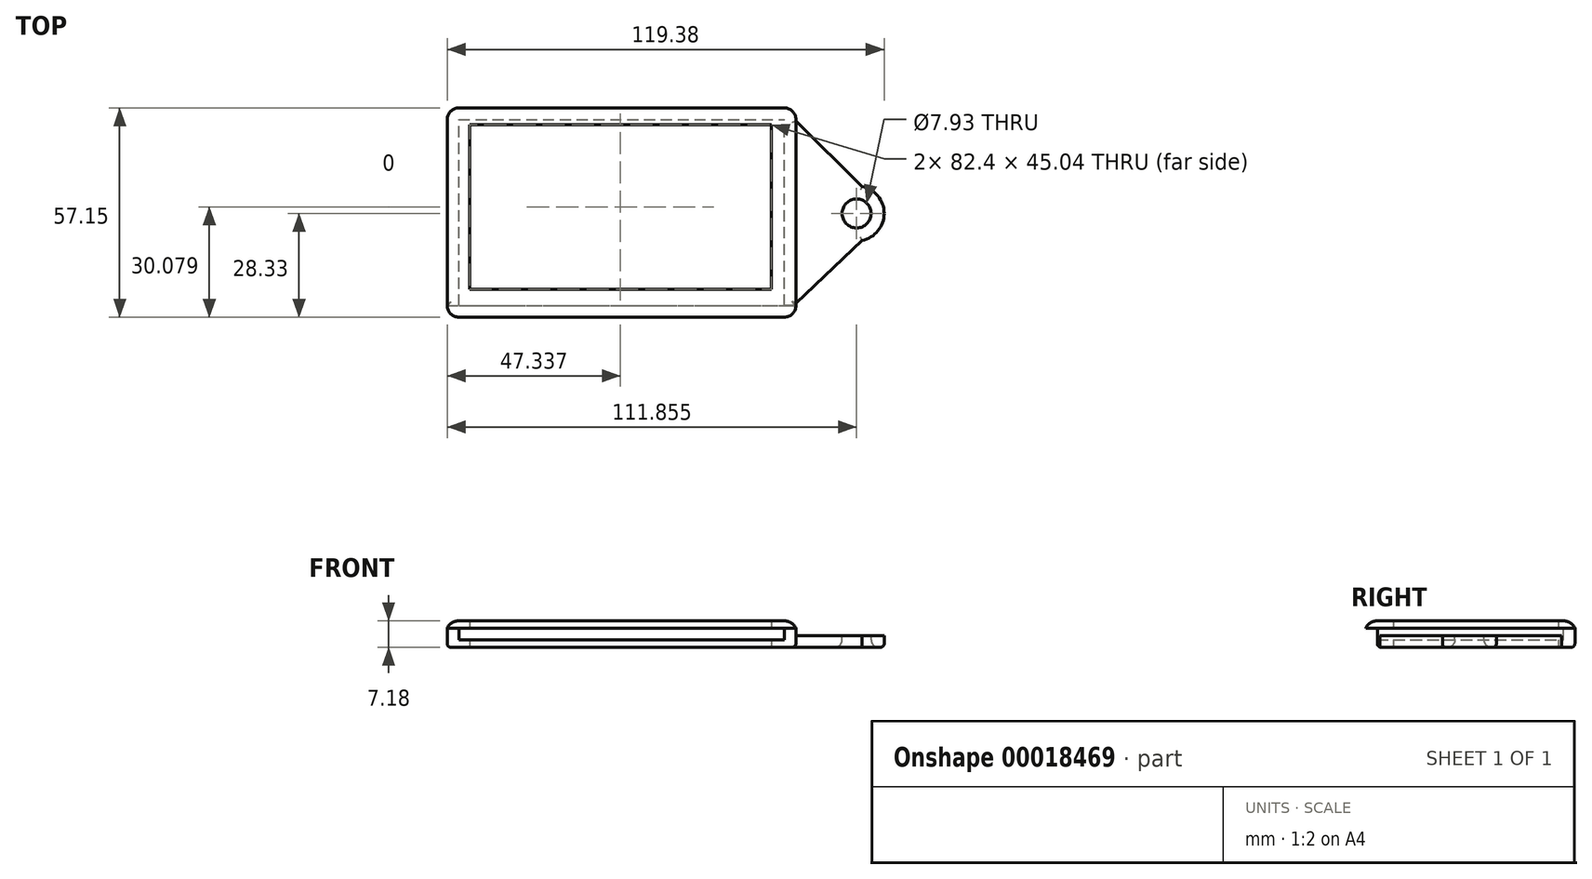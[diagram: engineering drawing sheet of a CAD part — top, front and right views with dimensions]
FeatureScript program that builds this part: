
annotation { "Feature Type Name" : "Feature", "Feature Type Description" : "" }
export const myFeature = defineFeature(function(context is Context, id is Id, definition is map)
    precondition{}
    {
        {
            var Q0;
            Q0=qCreatedBy(makeId("Top.planeOp"),FACE);
            var sketch = newSketch(context, id + "F0", { "sketchPlane" : qUnion([Q0])});
            skLineSegment(sketch, "E0.bottom", {"start": v(60.29, -16.12) * mm, "end": v(-28.61, -16.12) * mm});
            skLineSegment(sketch, "E0.top", {"start": v(60.29, 41.03) * mm, "end": v(-28.61, 41.03) * mm});
            skLineSegment(sketch, "E0.left", {"start": v(63.46, -12.94) * mm, "end": v(63.46, 37.86) * mm});
            skLineSegment(sketch, "E0.right", {"start": v(-31.79, -12.94) * mm, "end": v(-31.79, 37.86) * mm});
            skPoint(sketch, "E1.visualSharp", {"position": v(63.46, -16.12) * mm});
            skArc(sketch, "E1.filletArc", {"start": v(60.29, -16.12) * mm, "mid": v(62.53, -15.19) * mm, "end": v(63.46, -12.94) * mm});
            skPoint(sketch, "E2.visualSharp", {"position": v(-31.79, -16.12) * mm});
            skArc(sketch, "E2.filletArc", {"start": v(-31.79, -12.94) * mm, "mid": v(-30.86, -15.19) * mm, "end": v(-28.61, -16.12) * mm});
            skPoint(sketch, "E3.visualSharp", {"position": v(-31.79, 41.03) * mm});
            skArc(sketch, "E3.filletArc", {"start": v(-28.61, 41.03) * mm, "mid": v(-30.86, 40.1) * mm, "end": v(-31.79, 37.86) * mm});
            skPoint(sketch, "E4.visualSharp", {"position": v(63.46, 41.03) * mm});
            skArc(sketch, "E4.filletArc", {"start": v(63.46, 37.86) * mm, "mid": v(62.53, 40.1) * mm, "end": v(60.29, 41.03) * mm});
            skSolve(sketch);
        }
        {
            var Q0;
            Q0=makeQuery(id+"F0.imprint","IMPRINT",FACE,{"disambiguationData":[TD([[makeQuery(id+"F0.imprint","IMPRINT",EDGE,{"derivedFrom":sQuery(id+"F0.wireOp",EDGE,"E0.bottom")}),-1.0]])]});
            var Q1;
            Q1=makeQuery(id+"F0.imprint","IMPRINT",FACE,{"disambiguationData":[TD([[makeQuery(id+"F0.imprint","IMPRINT",EDGE,{"derivedFrom":sQuery(id+"F0.wireOp",EDGE,"E1.filletArc")}),1.0]])]});
            extrude(context, id + "F1", {"entities" : qUnion([Q0, Q1]), "depth" : 2 * mm});
        }
        {
            var Q0;
            Q0=makeQuery(id+"F1.opExtrude","CAP_FACE",FACE,{"disambiguationData":[OSD([sQuery(id+"F0.wireOp",EDGE,"E1.filletArc"),sQuery(id+"F0.wireOp",EDGE,"E2.filletArc"),sQuery(id+"F0.wireOp",EDGE,"E3.filletArc"),sQuery(id+"F0.wireOp",EDGE,"E4.filletArc"),sQuery(id+"F0.wireOp",EDGE,"E0.bottom"),sQuery(id+"F0.wireOp",EDGE,"E0.top"),sQuery(id+"F0.wireOp",EDGE,"E0.left"),sQuery(id+"F0.wireOp",EDGE,"E0.right")])],"isStart":false});
            fillet(context, id + "F2", {"entities" : qUnion([Q0]), "radius" : 3.17 * mm, "tangentPropagation" : true, "allowEdgeOverflow" : false});
        }
        {
            var Q0;
            Q0=makeQuery(id+"F1.opExtrude","SWEPT_BODY",BODY,{"disambiguationData":[OSD([sQuery(id+"F0.wireOp",EDGE,"E1.filletArc"),sQuery(id+"F0.wireOp",EDGE,"E2.filletArc"),sQuery(id+"F0.wireOp",EDGE,"E3.filletArc"),sQuery(id+"F0.wireOp",EDGE,"E4.filletArc"),sQuery(id+"F0.wireOp",EDGE,"E0.bottom"),sQuery(id+"F0.wireOp",EDGE,"E0.top"),sQuery(id+"F0.wireOp",EDGE,"E0.left"),sQuery(id+"F0.wireOp",EDGE,"E0.right")])]});
            transform(context, id + "F3", {"entities" : qUnion([Q0]), "transformType" : TransformType.TRANSLATION_3D, "dx" : -16.48 * mm, "dy" : -12.22 * mm, "dz" : 0 * mm, "makeCopy" : false});
        }
        {
            var Q0;
            Q0=makeQuery(id+"F1.opExtrude","CAP_FACE",FACE,{"disambiguationData":[OSD([sQuery(id+"F0.wireOp",EDGE,"E1.filletArc"),sQuery(id+"F0.wireOp",EDGE,"E2.filletArc"),sQuery(id+"F0.wireOp",EDGE,"E3.filletArc"),sQuery(id+"F0.wireOp",EDGE,"E4.filletArc"),sQuery(id+"F0.wireOp",EDGE,"E0.bottom"),sQuery(id+"F0.wireOp",EDGE,"E0.top"),sQuery(id+"F0.wireOp",EDGE,"E0.left"),sQuery(id+"F0.wireOp",EDGE,"E0.right")])],"isStart":false});
            var sketch = newSketch(context, id + "F4", { "sketchPlane" : qUnion([Q0])});
            skLineSegment(sketch, "E5", {"start": v(-19.47, 0.13) * mm, "end": v(-18.94, 8.61) * mm});
            skLineSegment(sketch, "E6", {"start": v(-18.94, 8.61) * mm, "end": v(-18.87, 8.63) * mm});
            skLineSegment(sketch, "E7", {"start": v(-18.87, 8.63) * mm, "end": v(-14.96, 8.63) * mm});
            skLineSegment(sketch, "E8", {"start": v(-14.96, 8.63) * mm, "end": v(-14.96, 8.48) * mm});
            skLineSegment(sketch, "E9", {"start": v(-14.96, 8.48) * mm, "end": v(-15.8, 0.4) * mm});
            skLineSegment(sketch, "E10", {"start": v(-15.8, 0.4) * mm, "end": v(-15.77, 0.38) * mm});
            skLineSegment(sketch, "E11", {"start": v(-15.77, 0.38) * mm, "end": v(-13.92, 0.52) * mm});
            skLineSegment(sketch, "E12", {"start": v(-13.92, 0.52) * mm, "end": v(-13.91, 0.56) * mm});
            skLineSegment(sketch, "E13", {"start": v(-13.91, 0.56) * mm, "end": v(-13.91, 3.27) * mm});
            skLineSegment(sketch, "E14", {"start": v(-13.91, 3.27) * mm, "end": v(-13.9, 3.67) * mm});
            skLineSegment(sketch, "E15", {"start": v(-13.9, 3.67) * mm, "end": v(-13.87, 4.23) * mm});
            skLineSegment(sketch, "E16", {"start": v(-13.87, 4.23) * mm, "end": v(-13.82, 4.74) * mm});
            skLineSegment(sketch, "E17", {"start": v(-13.82, 4.74) * mm, "end": v(-13.73, 5.21) * mm});
            skLineSegment(sketch, "E18", {"start": v(-13.73, 5.21) * mm, "end": v(-13.63, 5.65) * mm});
            skLineSegment(sketch, "E19", {"start": v(-13.63, 5.65) * mm, "end": v(-13.5, 6.04) * mm});
            skLineSegment(sketch, "E20", {"start": v(-13.5, 6.04) * mm, "end": v(-13.36, 6.4) * mm});
            skLineSegment(sketch, "E21", {"start": v(-13.36, 6.4) * mm, "end": v(-13.2, 6.73) * mm});
            skLineSegment(sketch, "E22", {"start": v(-13.2, 6.73) * mm, "end": v(-13.03, 7.02) * mm});
            skLineSegment(sketch, "E23", {"start": v(-13.03, 7.02) * mm, "end": v(-12.85, 7.28) * mm});
            skLineSegment(sketch, "E24", {"start": v(-12.85, 7.28) * mm, "end": v(-12.65, 7.5) * mm});
            skLineSegment(sketch, "E25", {"start": v(-12.65, 7.5) * mm, "end": v(-12.45, 7.71) * mm});
            skLineSegment(sketch, "E26", {"start": v(-12.45, 7.71) * mm, "end": v(-12.24, 7.9) * mm});
            skLineSegment(sketch, "E27", {"start": v(-12.24, 7.9) * mm, "end": v(-12.03, 8.05) * mm});
            skLineSegment(sketch, "E28", {"start": v(-12.03, 8.05) * mm, "end": v(-11.81, 8.18) * mm});
            skLineSegment(sketch, "E29", {"start": v(-11.81, 8.18) * mm, "end": v(-11.6, 8.29) * mm});
            skLineSegment(sketch, "E30", {"start": v(-11.6, 8.29) * mm, "end": v(-11.39, 8.38) * mm});
            skLineSegment(sketch, "E31", {"start": v(-11.39, 8.38) * mm, "end": v(-11.18, 8.45) * mm});
            skLineSegment(sketch, "E32", {"start": v(-11.18, 8.45) * mm, "end": v(-10.98, 8.51) * mm});
            skLineSegment(sketch, "E33", {"start": v(-10.98, 8.51) * mm, "end": v(-10.78, 8.56) * mm});
            skLineSegment(sketch, "E34", {"start": v(-10.78, 8.56) * mm, "end": v(-10.6, 8.59) * mm});
            skLineSegment(sketch, "E35", {"start": v(-10.6, 8.59) * mm, "end": v(-10.43, 8.61) * mm});
            skLineSegment(sketch, "E36", {"start": v(-10.43, 8.61) * mm, "end": v(-10.27, 8.63) * mm});
            skLineSegment(sketch, "E37", {"start": v(-10.27, 8.63) * mm, "end": v(-9.72, 8.63) * mm});
            skLineSegment(sketch, "E38", {"start": v(-9.72, 8.63) * mm, "end": v(-2.96, 8.63) * mm});
            skLineSegment(sketch, "E39", {"start": v(-2.96, 8.63) * mm, "end": v(-2.92, 8.55) * mm});
            skLineSegment(sketch, "E40", {"start": v(-2.92, 8.55) * mm, "end": v(-2.92, 1.78) * mm});
            skLineSegment(sketch, "E41", {"start": v(-2.92, 1.78) * mm, "end": v(-2.73, 1.8) * mm});
            skLineSegment(sketch, "E42", {"start": v(-2.73, 1.8) * mm, "end": v(-1.76, 1.95) * mm});
            skLineSegment(sketch, "E43", {"start": v(-1.76, 1.95) * mm, "end": v(-1.69, 2.11) * mm});
            skLineSegment(sketch, "E44", {"start": v(-1.69, 2.11) * mm, "end": v(-1.7, 2.42) * mm});
            skLineSegment(sketch, "E45", {"start": v(-1.7, 2.42) * mm, "end": v(-1.7, 2.74) * mm});
            skLineSegment(sketch, "E46", {"start": v(-1.7, 2.74) * mm, "end": v(-1.7, 3.08) * mm});
            skLineSegment(sketch, "E47", {"start": v(-1.7, 3.08) * mm, "end": v(-1.68, 3.43) * mm});
            skLineSegment(sketch, "E48", {"start": v(-1.68, 3.43) * mm, "end": v(-1.66, 3.78) * mm});
            skLineSegment(sketch, "E49", {"start": v(-1.66, 3.78) * mm, "end": v(-1.62, 4.15) * mm});
            skLineSegment(sketch, "E50", {"start": v(-1.62, 4.15) * mm, "end": v(-1.57, 4.51) * mm});
            skLineSegment(sketch, "E51", {"start": v(-1.57, 4.51) * mm, "end": v(-1.5, 4.88) * mm});
            skLineSegment(sketch, "E52", {"start": v(-1.5, 4.88) * mm, "end": v(-1.42, 5.25) * mm});
            skLineSegment(sketch, "E53", {"start": v(-1.42, 5.25) * mm, "end": v(-1.3, 5.6) * mm});
            skLineSegment(sketch, "E54", {"start": v(-1.3, 5.6) * mm, "end": v(-1.18, 5.96) * mm});
            skLineSegment(sketch, "E55", {"start": v(-1.18, 5.96) * mm, "end": v(-1.02, 6.3) * mm});
            skLineSegment(sketch, "E56", {"start": v(-1.02, 6.3) * mm, "end": v(-0.84, 6.63) * mm});
            skLineSegment(sketch, "E57", {"start": v(-0.84, 6.63) * mm, "end": v(-0.63, 6.94) * mm});
            skLineSegment(sketch, "E58", {"start": v(-0.63, 6.94) * mm, "end": v(-0.4, 7.24) * mm});
            skLineSegment(sketch, "E59", {"start": v(-0.4, 7.24) * mm, "end": v(-0.12, 7.5) * mm});
            skLineSegment(sketch, "E60", {"start": v(-0.12, 7.5) * mm, "end": v(0.19, 7.76) * mm});
            skLineSegment(sketch, "E61", {"start": v(0.19, 7.76) * mm, "end": v(0.53, 7.98) * mm});
            skLineSegment(sketch, "E62", {"start": v(0.53, 7.98) * mm, "end": v(0.91, 8.17) * mm});
            skLineSegment(sketch, "E63", {"start": v(0.91, 8.17) * mm, "end": v(1.33, 8.33) * mm});
            skLineSegment(sketch, "E64", {"start": v(1.33, 8.33) * mm, "end": v(1.8, 8.45) * mm});
            skLineSegment(sketch, "E65", {"start": v(1.8, 8.45) * mm, "end": v(2.3, 8.54) * mm});
            skLineSegment(sketch, "E66", {"start": v(2.3, 8.54) * mm, "end": v(2.86, 8.58) * mm});
            skLineSegment(sketch, "E67", {"start": v(2.86, 8.58) * mm, "end": v(3.44, 8.58) * mm});
            skLineSegment(sketch, "E68", {"start": v(3.44, 8.58) * mm, "end": v(3.97, 8.53) * mm});
            skLineSegment(sketch, "E69", {"start": v(3.97, 8.53) * mm, "end": v(4.45, 8.43) * mm});
            skLineSegment(sketch, "E70", {"start": v(4.45, 8.43) * mm, "end": v(4.9, 8.29) * mm});
            skLineSegment(sketch, "E71", {"start": v(4.9, 8.29) * mm, "end": v(5.28, 8.1) * mm});
            skLineSegment(sketch, "E72", {"start": v(5.28, 8.1) * mm, "end": v(5.64, 7.89) * mm});
            skLineSegment(sketch, "E73", {"start": v(5.64, 7.89) * mm, "end": v(5.95, 7.64) * mm});
            skLineSegment(sketch, "E74", {"start": v(5.95, 7.64) * mm, "end": v(6.22, 7.37) * mm});
            skLineSegment(sketch, "E75", {"start": v(6.22, 7.37) * mm, "end": v(6.47, 7.08) * mm});
            skLineSegment(sketch, "E76", {"start": v(6.47, 7.08) * mm, "end": v(6.67, 6.78) * mm});
            skLineSegment(sketch, "E77", {"start": v(6.67, 6.78) * mm, "end": v(6.85, 6.46) * mm});
            skLineSegment(sketch, "E78", {"start": v(6.85, 6.46) * mm, "end": v(7, 6.13) * mm});
            skLineSegment(sketch, "E79", {"start": v(7, 6.13) * mm, "end": v(7.13, 5.8) * mm});
            skLineSegment(sketch, "E80", {"start": v(7.13, 5.8) * mm, "end": v(7.23, 5.48) * mm});
            skLineSegment(sketch, "E81", {"start": v(7.23, 5.48) * mm, "end": v(7.31, 5.16) * mm});
            skLineSegment(sketch, "E82", {"start": v(7.31, 5.16) * mm, "end": v(7.37, 4.85) * mm});
            skLineSegment(sketch, "E83", {"start": v(7.37, 4.85) * mm, "end": v(7.42, 4.56) * mm});
            skLineSegment(sketch, "E84", {"start": v(7.42, 4.56) * mm, "end": v(7.45, 4.29) * mm});
            skLineSegment(sketch, "E85", {"start": v(7.45, 4.29) * mm, "end": v(7.47, 4.04) * mm});
            skLineSegment(sketch, "E86", {"start": v(7.47, 4.04) * mm, "end": v(7.48, 3.82) * mm});
            skLineSegment(sketch, "E87", {"start": v(7.48, 3.82) * mm, "end": v(7.49, 3.64) * mm});
            skLineSegment(sketch, "E88", {"start": v(7.49, 3.64) * mm, "end": v(7.48, 3.34) * mm});
            skLineSegment(sketch, "E89", {"start": v(7.48, 3.34) * mm, "end": v(7.5, 3.34) * mm});
            skLineSegment(sketch, "E90", {"start": v(7.5, 3.34) * mm, "end": v(9.28, 3.68) * mm});
            skLineSegment(sketch, "E91", {"start": v(9.28, 3.68) * mm, "end": v(9.3, 3.72) * mm});
            skLineSegment(sketch, "E92", {"start": v(9.3, 3.72) * mm, "end": v(8.78, 8.57) * mm});
            skLineSegment(sketch, "E93", {"start": v(8.78, 8.57) * mm, "end": v(8.8, 8.63) * mm});
            skLineSegment(sketch, "E94", {"start": v(8.8, 8.63) * mm, "end": v(12.67, 8.63) * mm});
            skLineSegment(sketch, "E95", {"start": v(12.67, 8.63) * mm, "end": v(12.73, 8.6) * mm});
            skLineSegment(sketch, "E96", {"start": v(12.73, 8.6) * mm, "end": v(13, 4.29) * mm});
            skLineSegment(sketch, "E97", {"start": v(13, 4.29) * mm, "end": v(13, 4.22) * mm});
            skLineSegment(sketch, "E98", {"start": v(13, 4.22) * mm, "end": v(14.22, 4.4) * mm});
            skLineSegment(sketch, "E99", {"start": v(14.22, 4.4) * mm, "end": v(14.24, 4.41) * mm});
            skLineSegment(sketch, "E100", {"start": v(14.24, 4.41) * mm, "end": v(14.43, 8.56) * mm});
            skLineSegment(sketch, "E101", {"start": v(14.43, 8.56) * mm, "end": v(14.45, 8.63) * mm});
            skLineSegment(sketch, "E102", {"start": v(14.45, 8.63) * mm, "end": v(18.42, 8.63) * mm});
            skLineSegment(sketch, "E103", {"start": v(18.42, 8.63) * mm, "end": v(18.5, 8.62) * mm});
            skLineSegment(sketch, "E104", {"start": v(18.5, 8.62) * mm, "end": v(18.13, 5.15) * mm});
            skLineSegment(sketch, "E105", {"start": v(18.13, 5.15) * mm, "end": v(18.14, 5.08) * mm});
            skLineSegment(sketch, "E106", {"start": v(18.14, 5.08) * mm, "end": v(24.47, 6.16) * mm});
            skLineSegment(sketch, "E107", {"start": v(24.47, 6.16) * mm, "end": v(24.6, 6.19) * mm});
            skLineSegment(sketch, "E108", {"start": v(24.6, 6.19) * mm, "end": v(24.6, 8.58) * mm});
            skLineSegment(sketch, "E109", {"start": v(24.6, 8.58) * mm, "end": v(24.61, 8.63) * mm});
            skLineSegment(sketch, "E110", {"start": v(24.61, 8.63) * mm, "end": v(29.13, 8.63) * mm});
            skLineSegment(sketch, "E111", {"start": v(29.13, 8.63) * mm, "end": v(29.23, 8.63) * mm});
            skLineSegment(sketch, "E112", {"start": v(29.23, 8.63) * mm, "end": v(29.23, 7.04) * mm});
            skLineSegment(sketch, "E113", {"start": v(29.23, 7.04) * mm, "end": v(30.8, 7.38) * mm});
            skLineSegment(sketch, "E114", {"start": v(30.8, 7.38) * mm, "end": v(30.84, 7.39) * mm});
            skLineSegment(sketch, "E115", {"start": v(30.84, 7.39) * mm, "end": v(30.84, 14.86) * mm});
            skLineSegment(sketch, "E116", {"start": v(30.84, 14.86) * mm, "end": v(30.81, 15.07) * mm});
            skLineSegment(sketch, "E117", {"start": v(30.81, 15.07) * mm, "end": v(-32.69, 15.07) * mm});
            skLineSegment(sketch, "E118", {"start": v(-32.69, 15.07) * mm, "end": v(-32.74, 6.1) * mm});
            skLineSegment(sketch, "E119", {"start": v(-32.74, 6.1) * mm, "end": v(-32.73, 5.93) * mm});
            skLineSegment(sketch, "E120", {"start": v(-32.73, 5.93) * mm, "end": v(-32.7, 5.75) * mm});
            skLineSegment(sketch, "E121", {"start": v(-32.7, 5.75) * mm, "end": v(-32.67, 5.57) * mm});
            skLineSegment(sketch, "E122", {"start": v(-32.67, 5.57) * mm, "end": v(-32.62, 5.4) * mm});
            skLineSegment(sketch, "E123", {"start": v(-32.62, 5.4) * mm, "end": v(-32.56, 5.22) * mm});
            skLineSegment(sketch, "E124", {"start": v(-32.56, 5.22) * mm, "end": v(-32.48, 5.04) * mm});
            skLineSegment(sketch, "E125", {"start": v(-32.48, 5.04) * mm, "end": v(-32.4, 4.87) * mm});
            skLineSegment(sketch, "E126", {"start": v(-32.4, 4.87) * mm, "end": v(-32.31, 4.7) * mm});
            skLineSegment(sketch, "E127", {"start": v(-32.31, 4.7) * mm, "end": v(-32.22, 4.53) * mm});
            skLineSegment(sketch, "E128", {"start": v(-32.22, 4.53) * mm, "end": v(-32.12, 4.37) * mm});
            skLineSegment(sketch, "E129", {"start": v(-32.12, 4.37) * mm, "end": v(-32.02, 4.21) * mm});
            skLineSegment(sketch, "E130", {"start": v(-32.02, 4.21) * mm, "end": v(-31.92, 4.06) * mm});
            skLineSegment(sketch, "E131", {"start": v(-31.92, 4.06) * mm, "end": v(-31.82, 3.92) * mm});
            skLineSegment(sketch, "E132", {"start": v(-31.82, 3.92) * mm, "end": v(-31.72, 3.79) * mm});
            skLineSegment(sketch, "E133", {"start": v(-31.72, 3.79) * mm, "end": v(-31.53, 3.55) * mm});
            skLineSegment(sketch, "E134", {"start": v(-31.53, 3.55) * mm, "end": v(-31.36, 3.35) * mm});
            skLineSegment(sketch, "E135", {"start": v(-31.36, 3.35) * mm, "end": v(-31.1, 3.08) * mm});
            skLineSegment(sketch, "E136", {"start": v(-31.1, 3.08) * mm, "end": v(-31, 3.08) * mm});
            skLineSegment(sketch, "E137", {"start": v(-31, 3.08) * mm, "end": v(-30.99, 8.63) * mm});
            skLineSegment(sketch, "E138", {"start": v(-30.99, 8.63) * mm, "end": v(-27.17, 8.63) * mm});
            skLineSegment(sketch, "E139", {"start": v(-27.17, 8.63) * mm, "end": v(-27.17, 1.68) * mm});
            skLineSegment(sketch, "E140", {"start": v(-27.17, 1.68) * mm, "end": v(-26.96, 0.75) * mm});
            skLineSegment(sketch, "E141", {"start": v(-26.96, 0.75) * mm, "end": v(-23.9, 0.36) * mm});
            skLineSegment(sketch, "E142", {"start": v(-23.9, 0.36) * mm, "end": v(-25, 8.63) * mm});
            skLineSegment(sketch, "E143", {"start": v(-25, 8.63) * mm, "end": v(-24.9, 8.63) * mm});
            skLineSegment(sketch, "E144", {"start": v(-24.9, 8.63) * mm, "end": v(-20.71, 8.63) * mm});
            skLineSegment(sketch, "E145", {"start": v(-20.71, 8.63) * mm, "end": v(-20.7, 8.44) * mm});
            skLineSegment(sketch, "E146", {"start": v(-20.7, 8.44) * mm, "end": v(-20.23, 0.14) * mm});
            skLineSegment(sketch, "E147", {"start": v(-20.23, 0.14) * mm, "end": v(-20.22, 0.13) * mm});
            skLineSegment(sketch, "E148", {"start": v(-20.22, 0.13) * mm, "end": v(-19.47, 0.13) * mm});
            skLineSegment(sketch, "E149", {"start": v(-20.02, -2.51) * mm, "end": v(-19.21, -2.5) * mm});
            skLineSegment(sketch, "E150", {"start": v(-19.21, -2.5) * mm, "end": v(-16.96, -2.41) * mm});
            skLineSegment(sketch, "E151", {"start": v(-16.96, -2.41) * mm, "end": v(-16.7, -2.4) * mm});
            skLineSegment(sketch, "E152", {"start": v(-16.7, -2.4) * mm, "end": v(-14.72, -2.33) * mm});
            skLineSegment(sketch, "E153", {"start": v(-14.72, -2.33) * mm, "end": v(-12.56, -2.21) * mm});
            skLineSegment(sketch, "E154", {"start": v(-12.56, -2.21) * mm, "end": v(-10.25, -2.05) * mm});
            skLineSegment(sketch, "E155", {"start": v(-10.25, -2.05) * mm, "end": v(-7.8, -1.84) * mm});
            skLineSegment(sketch, "E156", {"start": v(-7.8, -1.84) * mm, "end": v(-5.23, -1.6) * mm});
            skLineSegment(sketch, "E157", {"start": v(-5.23, -1.6) * mm, "end": v(-2.58, -1.34) * mm});
            skLineSegment(sketch, "E158", {"start": v(-2.58, -1.34) * mm, "end": v(0.14, -1.05) * mm});
            skLineSegment(sketch, "E159", {"start": v(0.14, -1.05) * mm, "end": v(2.9, -0.73) * mm});
            skLineSegment(sketch, "E160", {"start": v(2.9, -0.73) * mm, "end": v(5.67, -0.4) * mm});
            skLineSegment(sketch, "E161", {"start": v(5.67, -0.4) * mm, "end": v(8.44, -0.07) * mm});
            skLineSegment(sketch, "E162", {"start": v(8.44, -0.07) * mm, "end": v(11.18, 0.28) * mm});
            skLineSegment(sketch, "E163", {"start": v(11.18, 0.28) * mm, "end": v(13.86, 0.63) * mm});
            skLineSegment(sketch, "E164", {"start": v(13.86, 0.63) * mm, "end": v(16.47, 0.98) * mm});
            skLineSegment(sketch, "E165", {"start": v(16.47, 0.98) * mm, "end": v(18.97, 1.32) * mm});
            skLineSegment(sketch, "E166", {"start": v(18.97, 1.32) * mm, "end": v(21.35, 1.65) * mm});
            skLineSegment(sketch, "E167", {"start": v(21.35, 1.65) * mm, "end": v(23.58, 1.96) * mm});
            skLineSegment(sketch, "E168", {"start": v(23.58, 1.96) * mm, "end": v(25.63, 2.26) * mm});
            skLineSegment(sketch, "E169", {"start": v(25.63, 2.26) * mm, "end": v(29.13, 2.77) * mm});
            skLineSegment(sketch, "E170", {"start": v(29.13, 2.77) * mm, "end": v(33.18, 3.38) * mm});
            skLineSegment(sketch, "E171", {"start": v(33.18, 3.38) * mm, "end": v(33.32, 3.45) * mm});
            skLineSegment(sketch, "E172", {"start": v(33.32, 3.45) * mm, "end": v(33.44, 3.55) * mm});
            skLineSegment(sketch, "E173", {"start": v(33.44, 3.55) * mm, "end": v(33.54, 3.66) * mm});
            skLineSegment(sketch, "E174", {"start": v(33.54, 3.66) * mm, "end": v(33.64, 3.8) * mm});
            skLineSegment(sketch, "E175", {"start": v(33.64, 3.8) * mm, "end": v(33.71, 3.95) * mm});
            skLineSegment(sketch, "E176", {"start": v(33.71, 3.95) * mm, "end": v(33.78, 4.1) * mm});
            skLineSegment(sketch, "E177", {"start": v(33.78, 4.1) * mm, "end": v(33.83, 4.28) * mm});
            skLineSegment(sketch, "E178", {"start": v(33.83, 4.28) * mm, "end": v(33.86, 4.46) * mm});
            skLineSegment(sketch, "E179", {"start": v(33.86, 4.46) * mm, "end": v(33.89, 4.65) * mm});
            skLineSegment(sketch, "E180", {"start": v(33.89, 4.65) * mm, "end": v(33.9, 4.84) * mm});
            skLineSegment(sketch, "E181", {"start": v(33.9, 4.84) * mm, "end": v(33.9, 5.02) * mm});
            skLineSegment(sketch, "E182", {"start": v(33.9, 5.02) * mm, "end": v(33.89, 5.21) * mm});
            skLineSegment(sketch, "E183", {"start": v(33.89, 5.21) * mm, "end": v(33.87, 5.4) * mm});
            skLineSegment(sketch, "E184", {"start": v(33.87, 5.4) * mm, "end": v(33.83, 5.57) * mm});
            skLineSegment(sketch, "E185", {"start": v(33.83, 5.57) * mm, "end": v(33.8, 5.74) * mm});
            skLineSegment(sketch, "E186", {"start": v(33.8, 5.74) * mm, "end": v(33.74, 5.9) * mm});
            skLineSegment(sketch, "E187", {"start": v(33.74, 5.9) * mm, "end": v(33.68, 6.04) * mm});
            skLineSegment(sketch, "E188", {"start": v(33.68, 6.04) * mm, "end": v(33.61, 6.17) * mm});
            skLineSegment(sketch, "E189", {"start": v(33.61, 6.17) * mm, "end": v(33.54, 6.28) * mm});
            skLineSegment(sketch, "E190", {"start": v(33.54, 6.28) * mm, "end": v(33.45, 6.37) * mm});
            skLineSegment(sketch, "E191", {"start": v(33.45, 6.37) * mm, "end": v(33.36, 6.43) * mm});
            skLineSegment(sketch, "E192", {"start": v(33.36, 6.43) * mm, "end": v(33.27, 6.47) * mm});
            skLineSegment(sketch, "E193", {"start": v(33.27, 6.47) * mm, "end": v(33.17, 6.48) * mm});
            skLineSegment(sketch, "E194", {"start": v(33.17, 6.48) * mm, "end": v(31.1, 6.08) * mm});
            skLineSegment(sketch, "E195", {"start": v(31.1, 6.08) * mm, "end": v(28.94, 5.66) * mm});
            skLineSegment(sketch, "E196", {"start": v(28.94, 5.66) * mm, "end": v(26.84, 5.26) * mm});
            skLineSegment(sketch, "E197", {"start": v(26.84, 5.26) * mm, "end": v(24.8, 4.87) * mm});
            skLineSegment(sketch, "E198", {"start": v(24.8, 4.87) * mm, "end": v(22.84, 4.5) * mm});
            skLineSegment(sketch, "E199", {"start": v(22.84, 4.5) * mm, "end": v(20.93, 4.16) * mm});
            skLineSegment(sketch, "E200", {"start": v(20.93, 4.16) * mm, "end": v(19.08, 3.83) * mm});
            skLineSegment(sketch, "E201", {"start": v(19.08, 3.83) * mm, "end": v(17.29, 3.51) * mm});
            skLineSegment(sketch, "E202", {"start": v(17.29, 3.51) * mm, "end": v(15.56, 3.21) * mm});
            skLineSegment(sketch, "E203", {"start": v(15.56, 3.21) * mm, "end": v(13.88, 2.92) * mm});
            skLineSegment(sketch, "E204", {"start": v(13.88, 2.92) * mm, "end": v(12.26, 2.65) * mm});
            skLineSegment(sketch, "E205", {"start": v(12.26, 2.65) * mm, "end": v(10.7, 2.4) * mm});
            skLineSegment(sketch, "E206", {"start": v(10.7, 2.4) * mm, "end": v(9.19, 2.15) * mm});
            skLineSegment(sketch, "E207", {"start": v(9.19, 2.15) * mm, "end": v(7.73, 1.91) * mm});
            skLineSegment(sketch, "E208", {"start": v(7.73, 1.91) * mm, "end": v(6.32, 1.7) * mm});
            skLineSegment(sketch, "E209", {"start": v(6.32, 1.7) * mm, "end": v(4.96, 1.48) * mm});
            skLineSegment(sketch, "E210", {"start": v(4.96, 1.48) * mm, "end": v(3.66, 1.28) * mm});
            skLineSegment(sketch, "E211", {"start": v(3.66, 1.28) * mm, "end": v(1.19, 0.92) * mm});
            skLineSegment(sketch, "E212", {"start": v(1.19, 0.92) * mm, "end": v(-1.1, 0.59) * mm});
            skLineSegment(sketch, "E213", {"start": v(-1.1, 0.59) * mm, "end": v(-3.22, 0.3) * mm});
            skLineSegment(sketch, "E214", {"start": v(-3.22, 0.3) * mm, "end": v(-4.2, 0.15) * mm});
            skLineSegment(sketch, "E215", {"start": v(-4.2, 0.15) * mm, "end": v(-6.21, -0.14) * mm});
            skLineSegment(sketch, "E216", {"start": v(-6.21, -0.14) * mm, "end": v(-8.47, -0.45) * mm});
            skLineSegment(sketch, "E217", {"start": v(-8.47, -0.45) * mm, "end": v(-10.62, -0.71) * mm});
            skLineSegment(sketch, "E218", {"start": v(-10.62, -0.71) * mm, "end": v(-12.67, -0.93) * mm});
            skLineSegment(sketch, "E219", {"start": v(-12.67, -0.93) * mm, "end": v(-14.6, -1.11) * mm});
            skLineSegment(sketch, "E220", {"start": v(-14.6, -1.11) * mm, "end": v(-16.45, -1.25) * mm});
            skLineSegment(sketch, "E221", {"start": v(-16.45, -1.25) * mm, "end": v(-18.18, -1.34) * mm});
            skLineSegment(sketch, "E222", {"start": v(-18.18, -1.34) * mm, "end": v(-19.82, -1.38) * mm});
            skLineSegment(sketch, "E223", {"start": v(-19.82, -1.38) * mm, "end": v(-21.36, -1.38) * mm});
            skLineSegment(sketch, "E224", {"start": v(-21.36, -1.38) * mm, "end": v(-22.8, -1.33) * mm});
            skLineSegment(sketch, "E225", {"start": v(-22.8, -1.33) * mm, "end": v(-24.15, -1.24) * mm});
            skLineSegment(sketch, "E226", {"start": v(-24.15, -1.24) * mm, "end": v(-25.4, -1.1) * mm});
            skLineSegment(sketch, "E227", {"start": v(-25.4, -1.1) * mm, "end": v(-26.57, -0.92) * mm});
            skLineSegment(sketch, "E228", {"start": v(-26.57, -0.92) * mm, "end": v(-27.64, -0.68) * mm});
            skLineSegment(sketch, "E229", {"start": v(-27.64, -0.68) * mm, "end": v(-28.62, -0.4) * mm});
            skLineSegment(sketch, "E230", {"start": v(-28.62, -0.4) * mm, "end": v(-29.51, -0.07) * mm});
            skLineSegment(sketch, "E231", {"start": v(-29.51, -0.07) * mm, "end": v(-30.32, 0.3) * mm});
            skLineSegment(sketch, "E232", {"start": v(-30.32, 0.3) * mm, "end": v(-31.04, 0.73) * mm});
            skLineSegment(sketch, "E233", {"start": v(-31.04, 0.73) * mm, "end": v(-31.67, 1.2) * mm});
            skLineSegment(sketch, "E234", {"start": v(-31.67, 1.2) * mm, "end": v(-32.22, 1.72) * mm});
            skLineSegment(sketch, "E235", {"start": v(-32.22, 1.72) * mm, "end": v(-32.7, 2.3) * mm});
            skLineSegment(sketch, "E236", {"start": v(-32.7, 2.3) * mm, "end": v(-33.08, 2.92) * mm});
            skLineSegment(sketch, "E237", {"start": v(-33.08, 2.92) * mm, "end": v(-33.4, 3.6) * mm});
            skLineSegment(sketch, "E238", {"start": v(-33.4, 3.6) * mm, "end": v(-33.63, 4.32) * mm});
            skLineSegment(sketch, "E239", {"start": v(-33.63, 4.32) * mm, "end": v(-33.7, 4.4) * mm});
            skLineSegment(sketch, "E240", {"start": v(-33.7, 4.4) * mm, "end": v(-33.68, 4.06) * mm});
            skLineSegment(sketch, "E241", {"start": v(-33.68, 4.06) * mm, "end": v(-33.64, 3.74) * mm});
            skLineSegment(sketch, "E242", {"start": v(-33.64, 3.74) * mm, "end": v(-33.58, 3.43) * mm});
            skLineSegment(sketch, "E243", {"start": v(-33.58, 3.43) * mm, "end": v(-33.5, 3.12) * mm});
            skLineSegment(sketch, "E244", {"start": v(-33.5, 3.12) * mm, "end": v(-33.4, 2.82) * mm});
            skLineSegment(sketch, "E245", {"start": v(-33.4, 2.82) * mm, "end": v(-33.28, 2.53) * mm});
            skLineSegment(sketch, "E246", {"start": v(-33.28, 2.53) * mm, "end": v(-33.14, 2.24) * mm});
            skLineSegment(sketch, "E247", {"start": v(-33.14, 2.24) * mm, "end": v(-32.98, 1.97) * mm});
            skLineSegment(sketch, "E248", {"start": v(-32.98, 1.97) * mm, "end": v(-32.8, 1.7) * mm});
            skLineSegment(sketch, "E249", {"start": v(-32.8, 1.7) * mm, "end": v(-32.62, 1.44) * mm});
            skLineSegment(sketch, "E250", {"start": v(-32.62, 1.44) * mm, "end": v(-32.41, 1.2) * mm});
            skLineSegment(sketch, "E251", {"start": v(-32.41, 1.2) * mm, "end": v(-32.2, 0.95) * mm});
            skLineSegment(sketch, "E252", {"start": v(-32.2, 0.95) * mm, "end": v(-31.97, 0.72) * mm});
            skLineSegment(sketch, "E253", {"start": v(-31.97, 0.72) * mm, "end": v(-31.73, 0.5) * mm});
            skLineSegment(sketch, "E254", {"start": v(-31.73, 0.5) * mm, "end": v(-31.48, 0.3) * mm});
            skLineSegment(sketch, "E255", {"start": v(-31.48, 0.3) * mm, "end": v(-31.22, 0.09) * mm});
            skLineSegment(sketch, "E256", {"start": v(-31.22, 0.09) * mm, "end": v(-30.95, -0.1) * mm});
            skLineSegment(sketch, "E257", {"start": v(-30.95, -0.1) * mm, "end": v(-30.67, -0.28) * mm});
            skLineSegment(sketch, "E258", {"start": v(-30.67, -0.28) * mm, "end": v(-30.4, -0.45) * mm});
            skLineSegment(sketch, "E259", {"start": v(-30.4, -0.45) * mm, "end": v(-30.1, -0.61) * mm});
            skLineSegment(sketch, "E260", {"start": v(-30.1, -0.61) * mm, "end": v(-29.81, -0.76) * mm});
            skLineSegment(sketch, "E261", {"start": v(-29.81, -0.76) * mm, "end": v(-29.52, -0.9) * mm});
            skLineSegment(sketch, "E262", {"start": v(-29.52, -0.9) * mm, "end": v(-29.22, -1.03) * mm});
            skLineSegment(sketch, "E263", {"start": v(-29.22, -1.03) * mm, "end": v(-28.74, -1.22) * mm});
            skLineSegment(sketch, "E264", {"start": v(-28.74, -1.22) * mm, "end": v(-28.52, -1.3) * mm});
            skLineSegment(sketch, "E265", {"start": v(-28.52, -1.3) * mm, "end": v(-28.3, -1.38) * mm});
            skLineSegment(sketch, "E266", {"start": v(-28.3, -1.38) * mm, "end": v(-28.08, -1.45) * mm});
            skLineSegment(sketch, "E267", {"start": v(-28.08, -1.45) * mm, "end": v(-27.85, -1.52) * mm});
            skLineSegment(sketch, "E268", {"start": v(-27.85, -1.52) * mm, "end": v(-27.63, -1.6) * mm});
            skLineSegment(sketch, "E269", {"start": v(-27.63, -1.6) * mm, "end": v(-27.41, -1.66) * mm});
            skLineSegment(sketch, "E270", {"start": v(-27.41, -1.66) * mm, "end": v(-26.97, -1.77) * mm});
            skLineSegment(sketch, "E271", {"start": v(-26.97, -1.77) * mm, "end": v(-26.52, -1.88) * mm});
            skLineSegment(sketch, "E272", {"start": v(-26.52, -1.88) * mm, "end": v(-26.07, -1.98) * mm});
            skLineSegment(sketch, "E273", {"start": v(-26.07, -1.98) * mm, "end": v(-25.61, -2.07) * mm});
            skLineSegment(sketch, "E274", {"start": v(-25.61, -2.07) * mm, "end": v(-25.15, -2.15) * mm});
            skLineSegment(sketch, "E275", {"start": v(-25.15, -2.15) * mm, "end": v(-24.69, -2.22) * mm});
            skLineSegment(sketch, "E276", {"start": v(-24.69, -2.22) * mm, "end": v(-24.22, -2.28) * mm});
            skLineSegment(sketch, "E277", {"start": v(-24.22, -2.28) * mm, "end": v(-23.51, -2.37) * mm});
            skLineSegment(sketch, "E278", {"start": v(-23.51, -2.37) * mm, "end": v(-22.73, -2.42) * mm});
            skLineSegment(sketch, "E279", {"start": v(-22.73, -2.42) * mm, "end": v(-21.7, -2.47) * mm});
            skLineSegment(sketch, "E280", {"start": v(-21.7, -2.47) * mm, "end": v(-20.75, -2.5) * mm});
            skLineSegment(sketch, "E281", {"start": v(-20.75, -2.5) * mm, "end": v(-20.2, -2.51) * mm});
            skLineSegment(sketch, "E282", {"start": v(-20.2, -2.51) * mm, "end": v(-20.02, -2.51) * mm});
            skLineSegment(sketch, "E283", {"start": v(2.46, 2.56) * mm, "end": v(3.5, 2.72) * mm});
            skLineSegment(sketch, "E284", {"start": v(3.5, 2.72) * mm, "end": v(3.5, 3.94) * mm});
            skLineSegment(sketch, "E285", {"start": v(3.5, 3.94) * mm, "end": v(3.5, 4.05) * mm});
            skLineSegment(sketch, "E286", {"start": v(3.5, 4.05) * mm, "end": v(3.48, 4.17) * mm});
            skLineSegment(sketch, "E287", {"start": v(3.48, 4.17) * mm, "end": v(3.46, 4.3) * mm});
            skLineSegment(sketch, "E288", {"start": v(3.46, 4.3) * mm, "end": v(3.43, 4.42) * mm});
            skLineSegment(sketch, "E289", {"start": v(3.43, 4.42) * mm, "end": v(3.4, 4.54) * mm});
            skLineSegment(sketch, "E290", {"start": v(3.4, 4.54) * mm, "end": v(3.36, 4.66) * mm});
            skLineSegment(sketch, "E291", {"start": v(3.36, 4.66) * mm, "end": v(3.3, 4.77) * mm});
            skLineSegment(sketch, "E292", {"start": v(3.3, 4.77) * mm, "end": v(3.28, 4.82) * mm});
            skLineSegment(sketch, "E293", {"start": v(3.28, 4.82) * mm, "end": v(3.25, 4.86) * mm});
            skLineSegment(sketch, "E294", {"start": v(3.25, 4.86) * mm, "end": v(3.22, 4.9) * mm});
            skLineSegment(sketch, "E295", {"start": v(3.22, 4.9) * mm, "end": v(3.18, 4.94) * mm});
            skLineSegment(sketch, "E296", {"start": v(3.18, 4.94) * mm, "end": v(3.15, 4.97) * mm});
            skLineSegment(sketch, "E297", {"start": v(3.15, 4.97) * mm, "end": v(3.11, 5) * mm});
            skLineSegment(sketch, "E298", {"start": v(3.11, 5) * mm, "end": v(3.07, 5.01) * mm});
            skLineSegment(sketch, "E299", {"start": v(3.07, 5.01) * mm, "end": v(3.03, 5.03) * mm});
            skLineSegment(sketch, "E300", {"start": v(3.03, 5.03) * mm, "end": v(2.99, 5.03) * mm});
            skLineSegment(sketch, "E301", {"start": v(2.99, 5.03) * mm, "end": v(2.93, 5.03) * mm});
            skLineSegment(sketch, "E302", {"start": v(2.93, 5.03) * mm, "end": v(2.88, 5.01) * mm});
            skLineSegment(sketch, "E303", {"start": v(2.88, 5.01) * mm, "end": v(2.83, 4.99) * mm});
            skLineSegment(sketch, "E304", {"start": v(2.83, 4.99) * mm, "end": v(2.79, 4.95) * mm});
            skLineSegment(sketch, "E305", {"start": v(2.79, 4.95) * mm, "end": v(2.74, 4.91) * mm});
            skLineSegment(sketch, "E306", {"start": v(2.74, 4.91) * mm, "end": v(2.7, 4.86) * mm});
            skLineSegment(sketch, "E307", {"start": v(2.7, 4.86) * mm, "end": v(2.67, 4.8) * mm});
            skLineSegment(sketch, "E308", {"start": v(2.67, 4.8) * mm, "end": v(2.64, 4.74) * mm});
            skLineSegment(sketch, "E309", {"start": v(2.64, 4.74) * mm, "end": v(2.61, 4.68) * mm});
            skLineSegment(sketch, "E310", {"start": v(2.61, 4.68) * mm, "end": v(2.59, 4.6) * mm});
            skLineSegment(sketch, "E311", {"start": v(2.59, 4.6) * mm, "end": v(2.54, 4.46) * mm});
            skLineSegment(sketch, "E312", {"start": v(2.54, 4.46) * mm, "end": v(2.51, 4.32) * mm});
            skLineSegment(sketch, "E313", {"start": v(2.51, 4.32) * mm, "end": v(2.48, 4.12) * mm});
            skLineSegment(sketch, "E314", {"start": v(2.48, 4.12) * mm, "end": v(2.45, 3.84) * mm});
            skLineSegment(sketch, "E315", {"start": v(2.45, 3.84) * mm, "end": v(2.45, 2.58) * mm});
            skLineSegment(sketch, "E316", {"start": v(2.45, 2.58) * mm, "end": v(2.46, 2.56) * mm});
            skLineSegment(sketch, "E317", {"start": v(-9.1, 1.05) * mm, "end": v(-7.6, 1.22) * mm});
            skLineSegment(sketch, "E318", {"start": v(-7.6, 1.22) * mm, "end": v(-7.57, 1.23) * mm});
            skLineSegment(sketch, "E319", {"start": v(-7.57, 1.23) * mm, "end": v(-7.57, 4.54) * mm});
            skLineSegment(sketch, "E320", {"start": v(-7.57, 4.54) * mm, "end": v(-8.12, 4.54) * mm});
            skLineSegment(sketch, "E321", {"start": v(-8.12, 4.54) * mm, "end": v(-8.22, 4.53) * mm});
            skLineSegment(sketch, "E322", {"start": v(-8.22, 4.53) * mm, "end": v(-8.33, 4.52) * mm});
            skLineSegment(sketch, "E323", {"start": v(-8.33, 4.52) * mm, "end": v(-8.43, 4.49) * mm});
            skLineSegment(sketch, "E324", {"start": v(-8.43, 4.49) * mm, "end": v(-8.52, 4.45) * mm});
            skLineSegment(sketch, "E325", {"start": v(-8.52, 4.45) * mm, "end": v(-8.6, 4.4) * mm});
            skLineSegment(sketch, "E326", {"start": v(-8.6, 4.4) * mm, "end": v(-8.67, 4.35) * mm});
            skLineSegment(sketch, "E327", {"start": v(-8.67, 4.35) * mm, "end": v(-8.74, 4.28) * mm});
            skLineSegment(sketch, "E328", {"start": v(-8.74, 4.28) * mm, "end": v(-8.8, 4.21) * mm});
            skLineSegment(sketch, "E329", {"start": v(-8.8, 4.21) * mm, "end": v(-8.85, 4.14) * mm});
            skLineSegment(sketch, "E330", {"start": v(-8.85, 4.14) * mm, "end": v(-8.9, 4.06) * mm});
            skLineSegment(sketch, "E331", {"start": v(-8.9, 4.06) * mm, "end": v(-8.94, 3.98) * mm});
            skLineSegment(sketch, "E332", {"start": v(-8.94, 3.98) * mm, "end": v(-8.97, 3.9) * mm});
            skLineSegment(sketch, "E333", {"start": v(-8.97, 3.9) * mm, "end": v(-9, 3.82) * mm});
            skLineSegment(sketch, "E334", {"start": v(-9, 3.82) * mm, "end": v(-9.03, 3.74) * mm});
            skLineSegment(sketch, "E335", {"start": v(-9.03, 3.74) * mm, "end": v(-9.06, 3.58) * mm});
            skLineSegment(sketch, "E336", {"start": v(-9.06, 3.58) * mm, "end": v(-9.09, 3.44) * mm});
            skLineSegment(sketch, "E337", {"start": v(-9.09, 3.44) * mm, "end": v(-9.1, 3.22) * mm});
            skLineSegment(sketch, "E338", {"start": v(-9.1, 3.22) * mm, "end": v(-9.1, 1.07) * mm});
            skLineSegment(sketch, "E339", {"start": v(-9.1, 1.07) * mm, "end": v(-9.1, 1.05) * mm});
            skLineSegment(sketch, "E340", {"start": v(29.25, -14.98) * mm, "end": v(29.25, 1.48) * mm});
            skLineSegment(sketch, "E341", {"start": v(29.25, 1.48) * mm, "end": v(24.59, 0.82) * mm});
            skLineSegment(sketch, "E342", {"start": v(24.59, 0.82) * mm, "end": v(24.58, -1.13) * mm});
            skLineSegment(sketch, "E343", {"start": v(24.58, -1.13) * mm, "end": v(24.06, -1.13) * mm});
            skLineSegment(sketch, "E344", {"start": v(24.06, -1.13) * mm, "end": v(21.66, -1.17) * mm});
            skLineSegment(sketch, "E345", {"start": v(21.66, -1.17) * mm, "end": v(21.38, -1.22) * mm});
            skLineSegment(sketch, "E346", {"start": v(21.38, -1.22) * mm, "end": v(21.12, -1.3) * mm});
            skLineSegment(sketch, "E347", {"start": v(21.12, -1.3) * mm, "end": v(20.87, -1.4) * mm});
            skLineSegment(sketch, "E348", {"start": v(20.87, -1.4) * mm, "end": v(20.64, -1.52) * mm});
            skLineSegment(sketch, "E349", {"start": v(20.64, -1.52) * mm, "end": v(20.42, -1.66) * mm});
            skLineSegment(sketch, "E350", {"start": v(20.42, -1.66) * mm, "end": v(20.21, -1.82) * mm});
            skLineSegment(sketch, "E351", {"start": v(20.21, -1.82) * mm, "end": v(20.02, -2) * mm});
            skLineSegment(sketch, "E352", {"start": v(20.02, -2) * mm, "end": v(19.84, -2.2) * mm});
            skLineSegment(sketch, "E353", {"start": v(19.84, -2.2) * mm, "end": v(19.67, -2.4) * mm});
            skLineSegment(sketch, "E354", {"start": v(19.67, -2.4) * mm, "end": v(19.52, -2.63) * mm});
            skLineSegment(sketch, "E355", {"start": v(19.52, -2.63) * mm, "end": v(19.38, -2.88) * mm});
            skLineSegment(sketch, "E356", {"start": v(19.38, -2.88) * mm, "end": v(19.25, -3.13) * mm});
            skLineSegment(sketch, "E357", {"start": v(19.25, -3.13) * mm, "end": v(19.13, -3.4) * mm});
            skLineSegment(sketch, "E358", {"start": v(19.13, -3.4) * mm, "end": v(19.03, -3.68) * mm});
            skLineSegment(sketch, "E359", {"start": v(19.03, -3.68) * mm, "end": v(18.94, -3.97) * mm});
            skLineSegment(sketch, "E360", {"start": v(18.94, -3.97) * mm, "end": v(18.86, -4.27) * mm});
            skLineSegment(sketch, "E361", {"start": v(18.86, -4.27) * mm, "end": v(18.8, -4.58) * mm});
            skLineSegment(sketch, "E362", {"start": v(18.8, -4.58) * mm, "end": v(18.74, -4.9) * mm});
            skLineSegment(sketch, "E363", {"start": v(18.74, -4.9) * mm, "end": v(18.7, -5.22) * mm});
            skLineSegment(sketch, "E364", {"start": v(18.7, -5.22) * mm, "end": v(18.66, -5.55) * mm});
            skLineSegment(sketch, "E365", {"start": v(18.66, -5.55) * mm, "end": v(18.64, -5.89) * mm});
            skLineSegment(sketch, "E366", {"start": v(18.64, -5.89) * mm, "end": v(18.63, -6.22) * mm});
            skLineSegment(sketch, "E367", {"start": v(18.63, -6.22) * mm, "end": v(18.63, -9.8) * mm});
            skLineSegment(sketch, "E368", {"start": v(18.63, -9.8) * mm, "end": v(18.63, -10.19) * mm});
            skLineSegment(sketch, "E369", {"start": v(18.63, -10.19) * mm, "end": v(18.66, -10.78) * mm});
            skLineSegment(sketch, "E370", {"start": v(18.66, -10.78) * mm, "end": v(18.74, -11.33) * mm});
            skLineSegment(sketch, "E371", {"start": v(18.74, -11.33) * mm, "end": v(18.84, -11.83) * mm});
            skLineSegment(sketch, "E372", {"start": v(18.84, -11.83) * mm, "end": v(18.98, -12.28) * mm});
            skLineSegment(sketch, "E373", {"start": v(18.98, -12.28) * mm, "end": v(19.14, -12.68) * mm});
            skLineSegment(sketch, "E374", {"start": v(19.14, -12.68) * mm, "end": v(19.32, -13.04) * mm});
            skLineSegment(sketch, "E375", {"start": v(19.32, -13.04) * mm, "end": v(19.53, -13.37) * mm});
            skLineSegment(sketch, "E376", {"start": v(19.53, -13.37) * mm, "end": v(19.75, -13.65) * mm});
            skLineSegment(sketch, "E377", {"start": v(19.75, -13.65) * mm, "end": v(19.98, -13.9) * mm});
            skLineSegment(sketch, "E378", {"start": v(19.98, -13.9) * mm, "end": v(20.23, -14.12) * mm});
            skLineSegment(sketch, "E379", {"start": v(20.23, -14.12) * mm, "end": v(20.48, -14.3) * mm});
            skLineSegment(sketch, "E380", {"start": v(20.48, -14.3) * mm, "end": v(20.73, -14.46) * mm});
            skLineSegment(sketch, "E381", {"start": v(20.73, -14.46) * mm, "end": v(20.98, -14.6) * mm});
            skLineSegment(sketch, "E382", {"start": v(20.98, -14.6) * mm, "end": v(21.22, -14.7) * mm});
            skLineSegment(sketch, "E383", {"start": v(21.22, -14.7) * mm, "end": v(21.46, -14.79) * mm});
            skLineSegment(sketch, "E384", {"start": v(21.46, -14.79) * mm, "end": v(21.69, -14.85) * mm});
            skLineSegment(sketch, "E385", {"start": v(21.69, -14.85) * mm, "end": v(21.9, -14.9) * mm});
            skLineSegment(sketch, "E386", {"start": v(21.9, -14.9) * mm, "end": v(22.1, -14.94) * mm});
            skLineSegment(sketch, "E387", {"start": v(22.1, -14.94) * mm, "end": v(22.26, -14.97) * mm});
            skLineSegment(sketch, "E388", {"start": v(22.26, -14.97) * mm, "end": v(29.08, -15) * mm});
            skLineSegment(sketch, "E389", {"start": v(29.08, -15) * mm, "end": v(29.25, -14.98) * mm});
            skLineSegment(sketch, "E390", {"start": v(23.6, -11.08) * mm, "end": v(23.49, -11.07) * mm});
            skLineSegment(sketch, "E391", {"start": v(23.49, -11.07) * mm, "end": v(23.38, -11.06) * mm});
            skLineSegment(sketch, "E392", {"start": v(23.38, -11.06) * mm, "end": v(23.28, -11.03) * mm});
            skLineSegment(sketch, "E393", {"start": v(23.28, -11.03) * mm, "end": v(23.2, -11) * mm});
            skLineSegment(sketch, "E394", {"start": v(23.2, -11) * mm, "end": v(23.1, -10.94) * mm});
            skLineSegment(sketch, "E395", {"start": v(23.1, -10.94) * mm, "end": v(23.04, -10.89) * mm});
            skLineSegment(sketch, "E396", {"start": v(23.04, -10.89) * mm, "end": v(22.97, -10.83) * mm});
            skLineSegment(sketch, "E397", {"start": v(22.97, -10.83) * mm, "end": v(22.9, -10.76) * mm});
            skLineSegment(sketch, "E398", {"start": v(22.9, -10.76) * mm, "end": v(22.86, -10.69) * mm});
            skLineSegment(sketch, "E399", {"start": v(22.86, -10.69) * mm, "end": v(22.81, -10.61) * mm});
            skLineSegment(sketch, "E400", {"start": v(22.81, -10.61) * mm, "end": v(22.77, -10.54) * mm});
            skLineSegment(sketch, "E401", {"start": v(22.77, -10.54) * mm, "end": v(22.74, -10.46) * mm});
            skLineSegment(sketch, "E402", {"start": v(22.74, -10.46) * mm, "end": v(22.7, -10.38) * mm});
            skLineSegment(sketch, "E403", {"start": v(22.7, -10.38) * mm, "end": v(22.68, -10.3) * mm});
            skLineSegment(sketch, "E404", {"start": v(22.68, -10.3) * mm, "end": v(22.66, -10.22) * mm});
            skLineSegment(sketch, "E405", {"start": v(22.66, -10.22) * mm, "end": v(22.63, -10.08) * mm});
            skLineSegment(sketch, "E406", {"start": v(22.63, -10.08) * mm, "end": v(22.61, -9.9) * mm});
            skLineSegment(sketch, "E407", {"start": v(22.61, -9.9) * mm, "end": v(22.6, -9.8) * mm});
            skLineSegment(sketch, "E408", {"start": v(22.6, -9.8) * mm, "end": v(22.6, -6.3) * mm});
            skLineSegment(sketch, "E409", {"start": v(22.6, -6.3) * mm, "end": v(22.62, -6.15) * mm});
            skLineSegment(sketch, "E410", {"start": v(22.62, -6.15) * mm, "end": v(22.64, -6) * mm});
            skLineSegment(sketch, "E411", {"start": v(22.64, -6) * mm, "end": v(22.66, -5.87) * mm});
            skLineSegment(sketch, "E412", {"start": v(22.66, -5.87) * mm, "end": v(22.7, -5.76) * mm});
            skLineSegment(sketch, "E413", {"start": v(22.7, -5.76) * mm, "end": v(22.74, -5.65) * mm});
            skLineSegment(sketch, "E414", {"start": v(22.74, -5.65) * mm, "end": v(22.79, -5.56) * mm});
            skLineSegment(sketch, "E415", {"start": v(22.79, -5.56) * mm, "end": v(22.84, -5.47) * mm});
            skLineSegment(sketch, "E416", {"start": v(22.84, -5.47) * mm, "end": v(22.9, -5.4) * mm});
            skLineSegment(sketch, "E417", {"start": v(22.9, -5.4) * mm, "end": v(22.95, -5.33) * mm});
            skLineSegment(sketch, "E418", {"start": v(22.95, -5.33) * mm, "end": v(23.01, -5.27) * mm});
            skLineSegment(sketch, "E419", {"start": v(23.01, -5.27) * mm, "end": v(23.07, -5.22) * mm});
            skLineSegment(sketch, "E420", {"start": v(23.07, -5.22) * mm, "end": v(23.14, -5.18) * mm});
            skLineSegment(sketch, "E421", {"start": v(23.14, -5.18) * mm, "end": v(23.2, -5.15) * mm});
            skLineSegment(sketch, "E422", {"start": v(23.2, -5.15) * mm, "end": v(23.26, -5.12) * mm});
            skLineSegment(sketch, "E423", {"start": v(23.26, -5.12) * mm, "end": v(23.32, -5.1) * mm});
            skLineSegment(sketch, "E424", {"start": v(23.32, -5.1) * mm, "end": v(23.38, -5.07) * mm});
            skLineSegment(sketch, "E425", {"start": v(23.38, -5.07) * mm, "end": v(23.47, -5.05) * mm});
            skLineSegment(sketch, "E426", {"start": v(23.47, -5.05) * mm, "end": v(23.61, -5.03) * mm});
            skLineSegment(sketch, "E427", {"start": v(23.61, -5.03) * mm, "end": v(24.55, -5.03) * mm});
            skLineSegment(sketch, "E428", {"start": v(24.55, -5.03) * mm, "end": v(24.57, -5.04) * mm});
            skLineSegment(sketch, "E429", {"start": v(24.57, -5.04) * mm, "end": v(24.57, -11.08) * mm});
            skLineSegment(sketch, "E430", {"start": v(24.57, -11.08) * mm, "end": v(23.6, -11.08) * mm});
            skLineSegment(sketch, "E431", {"start": v(16.47, -11) * mm, "end": v(17.59, -0.16) * mm});
            skLineSegment(sketch, "E432", {"start": v(17.59, -0.16) * mm, "end": v(14.02, -0.65) * mm});
            skLineSegment(sketch, "E433", {"start": v(14.02, -0.65) * mm, "end": v(13.68, -7.35) * mm});
            skLineSegment(sketch, "E434", {"start": v(13.68, -7.35) * mm, "end": v(13.27, -0.74) * mm});
            skLineSegment(sketch, "E435", {"start": v(13.27, -0.74) * mm, "end": v(9.84, -1.18) * mm});
            skLineSegment(sketch, "E436", {"start": v(9.84, -1.18) * mm, "end": v(10.87, -11) * mm});
            skLineSegment(sketch, "E437", {"start": v(10.87, -11) * mm, "end": v(16.47, -11) * mm});
            skLineSegment(sketch, "E438", {"start": v(-30.19, -10.95) * mm, "end": v(-29.14, -3.93) * mm});
            skLineSegment(sketch, "E439", {"start": v(-29.14, -3.93) * mm, "end": v(-29.12, -3.82) * mm});
            skLineSegment(sketch, "E440", {"start": v(-29.12, -3.82) * mm, "end": v(-28.08, -10.82) * mm});
            skLineSegment(sketch, "E441", {"start": v(-28.08, -10.82) * mm, "end": v(-28.05, -11) * mm});
            skLineSegment(sketch, "E442", {"start": v(-28.05, -11) * mm, "end": v(-24.35, -11) * mm});
            skLineSegment(sketch, "E443", {"start": v(-24.35, -11) * mm, "end": v(-26.06, -3.4) * mm});
            skLineSegment(sketch, "E444", {"start": v(-26.06, -3.4) * mm, "end": v(-26.07, -3.39) * mm});
            skLineSegment(sketch, "E445", {"start": v(-26.07, -3.39) * mm, "end": v(-26.45, -3.3) * mm});
            skLineSegment(sketch, "E446", {"start": v(-26.45, -3.3) * mm, "end": v(-26.8, -3.22) * mm});
            skLineSegment(sketch, "E447", {"start": v(-26.8, -3.22) * mm, "end": v(-27.25, -3.1) * mm});
            skLineSegment(sketch, "E448", {"start": v(-27.25, -3.1) * mm, "end": v(-27.5, -3.04) * mm});
            skLineSegment(sketch, "E449", {"start": v(-27.5, -3.04) * mm, "end": v(-27.76, -2.97) * mm});
            skLineSegment(sketch, "E450", {"start": v(-27.76, -2.97) * mm, "end": v(-28.03, -2.88) * mm});
            skLineSegment(sketch, "E451", {"start": v(-28.03, -2.88) * mm, "end": v(-28.32, -2.8) * mm});
            skLineSegment(sketch, "E452", {"start": v(-28.32, -2.8) * mm, "end": v(-28.6, -2.7) * mm});
            skLineSegment(sketch, "E453", {"start": v(-28.6, -2.7) * mm, "end": v(-28.9, -2.59) * mm});
            skLineSegment(sketch, "E454", {"start": v(-28.9, -2.59) * mm, "end": v(-29.21, -2.47) * mm});
            skLineSegment(sketch, "E455", {"start": v(-29.21, -2.47) * mm, "end": v(-29.52, -2.35) * mm});
            skLineSegment(sketch, "E456", {"start": v(-29.52, -2.35) * mm, "end": v(-29.82, -2.22) * mm});
            skLineSegment(sketch, "E457", {"start": v(-29.82, -2.22) * mm, "end": v(-30.12, -2.08) * mm});
            skLineSegment(sketch, "E458", {"start": v(-30.12, -2.08) * mm, "end": v(-30.42, -1.94) * mm});
            skLineSegment(sketch, "E459", {"start": v(-30.42, -1.94) * mm, "end": v(-30.71, -1.78) * mm});
            skLineSegment(sketch, "E460", {"start": v(-30.71, -1.78) * mm, "end": v(-31, -1.62) * mm});
            skLineSegment(sketch, "E461", {"start": v(-31, -1.62) * mm, "end": v(-31.26, -1.45) * mm});
            skLineSegment(sketch, "E462", {"start": v(-31.26, -1.45) * mm, "end": v(-31.52, -1.27) * mm});
            skLineSegment(sketch, "E463", {"start": v(-31.52, -1.27) * mm, "end": v(-31.7, -1.69) * mm});
            skLineSegment(sketch, "E464", {"start": v(-31.7, -1.69) * mm, "end": v(-33.9, -11) * mm});
            skLineSegment(sketch, "E465", {"start": v(-33.9, -11) * mm, "end": v(-33.86, -11) * mm});
            skLineSegment(sketch, "E466", {"start": v(-33.86, -11) * mm, "end": v(-30.24, -11) * mm});
            skLineSegment(sketch, "E467", {"start": v(-30.24, -11) * mm, "end": v(-30.19, -10.95) * mm});
            skLineSegment(sketch, "E468", {"start": v(2.66, -11.36) * mm, "end": v(3.14, -11.37) * mm});
            skLineSegment(sketch, "E469", {"start": v(3.14, -11.37) * mm, "end": v(3.32, -11.35) * mm});
            skLineSegment(sketch, "E470", {"start": v(3.32, -11.35) * mm, "end": v(3.53, -11.33) * mm});
            skLineSegment(sketch, "E471", {"start": v(3.53, -11.33) * mm, "end": v(3.65, -11.32) * mm});
            skLineSegment(sketch, "E472", {"start": v(3.65, -11.32) * mm, "end": v(3.77, -11.3) * mm});
            skLineSegment(sketch, "E473", {"start": v(3.77, -11.3) * mm, "end": v(3.9, -11.27) * mm});
            skLineSegment(sketch, "E474", {"start": v(3.9, -11.27) * mm, "end": v(4.03, -11.25) * mm});
            skLineSegment(sketch, "E475", {"start": v(4.03, -11.25) * mm, "end": v(4.16, -11.21) * mm});
            skLineSegment(sketch, "E476", {"start": v(4.16, -11.21) * mm, "end": v(4.3, -11.17) * mm});
            skLineSegment(sketch, "E477", {"start": v(4.3, -11.17) * mm, "end": v(4.44, -11.13) * mm});
            skLineSegment(sketch, "E478", {"start": v(4.44, -11.13) * mm, "end": v(4.58, -11.07) * mm});
            skLineSegment(sketch, "E479", {"start": v(4.58, -11.07) * mm, "end": v(4.73, -11.02) * mm});
            skLineSegment(sketch, "E480", {"start": v(4.73, -11.02) * mm, "end": v(4.88, -10.95) * mm});
            skLineSegment(sketch, "E481", {"start": v(4.88, -10.95) * mm, "end": v(5.02, -10.88) * mm});
            skLineSegment(sketch, "E482", {"start": v(5.02, -10.88) * mm, "end": v(5.17, -10.8) * mm});
            skLineSegment(sketch, "E483", {"start": v(5.17, -10.8) * mm, "end": v(5.32, -10.7) * mm});
            skLineSegment(sketch, "E484", {"start": v(5.32, -10.7) * mm, "end": v(5.46, -10.6) * mm});
            skLineSegment(sketch, "E485", {"start": v(5.46, -10.6) * mm, "end": v(5.6, -10.5) * mm});
            skLineSegment(sketch, "E486", {"start": v(5.6, -10.5) * mm, "end": v(5.74, -10.38) * mm});
            skLineSegment(sketch, "E487", {"start": v(5.74, -10.38) * mm, "end": v(5.87, -10.26) * mm});
            skLineSegment(sketch, "E488", {"start": v(5.87, -10.26) * mm, "end": v(6, -10.13) * mm});
            skLineSegment(sketch, "E489", {"start": v(6, -10.13) * mm, "end": v(6.14, -9.98) * mm});
            skLineSegment(sketch, "E490", {"start": v(6.14, -9.98) * mm, "end": v(6.26, -9.83) * mm});
            skLineSegment(sketch, "E491", {"start": v(6.26, -9.83) * mm, "end": v(6.39, -9.68) * mm});
            skLineSegment(sketch, "E492", {"start": v(6.39, -9.68) * mm, "end": v(6.5, -9.5) * mm});
            skLineSegment(sketch, "E493", {"start": v(6.5, -9.5) * mm, "end": v(6.62, -9.33) * mm});
            skLineSegment(sketch, "E494", {"start": v(6.62, -9.33) * mm, "end": v(6.72, -9.15) * mm});
            skLineSegment(sketch, "E495", {"start": v(6.72, -9.15) * mm, "end": v(6.83, -8.95) * mm});
            skLineSegment(sketch, "E496", {"start": v(6.83, -8.95) * mm, "end": v(6.92, -8.75) * mm});
            skLineSegment(sketch, "E497", {"start": v(6.92, -8.75) * mm, "end": v(7.01, -8.54) * mm});
            skLineSegment(sketch, "E498", {"start": v(7.01, -8.54) * mm, "end": v(7.1, -8.32) * mm});
            skLineSegment(sketch, "E499", {"start": v(7.1, -8.32) * mm, "end": v(7.17, -8.1) * mm});
            skLineSegment(sketch, "E500", {"start": v(7.17, -8.1) * mm, "end": v(7.24, -7.86) * mm});
            skLineSegment(sketch, "E501", {"start": v(7.24, -7.86) * mm, "end": v(7.3, -7.61) * mm});
            skLineSegment(sketch, "E502", {"start": v(7.3, -7.61) * mm, "end": v(7.35, -7.36) * mm});
            skLineSegment(sketch, "E503", {"start": v(7.35, -7.36) * mm, "end": v(7.4, -7.1) * mm});
            skLineSegment(sketch, "E504", {"start": v(7.4, -7.1) * mm, "end": v(7.43, -6.83) * mm});
            skLineSegment(sketch, "E505", {"start": v(7.43, -6.83) * mm, "end": v(7.45, -6.55) * mm});
            skLineSegment(sketch, "E506", {"start": v(7.45, -6.55) * mm, "end": v(7.47, -6.26) * mm});
            skLineSegment(sketch, "E507", {"start": v(7.47, -6.26) * mm, "end": v(7.47, -5.99) * mm});
            skLineSegment(sketch, "E508", {"start": v(7.47, -5.99) * mm, "end": v(7.47, -1.47) * mm});
            skLineSegment(sketch, "E509", {"start": v(7.47, -1.47) * mm, "end": v(3.59, -1.92) * mm});
            skLineSegment(sketch, "E510", {"start": v(3.59, -1.92) * mm, "end": v(3.58, -7.11) * mm});
            skLineSegment(sketch, "E511", {"start": v(3.58, -7.11) * mm, "end": v(3.58, -7.2) * mm});
            skLineSegment(sketch, "E512", {"start": v(3.58, -7.2) * mm, "end": v(3.56, -7.38) * mm});
            skLineSegment(sketch, "E513", {"start": v(3.56, -7.38) * mm, "end": v(3.55, -7.45) * mm});
            skLineSegment(sketch, "E514", {"start": v(3.55, -7.45) * mm, "end": v(3.54, -7.53) * mm});
            skLineSegment(sketch, "E515", {"start": v(3.54, -7.53) * mm, "end": v(3.52, -7.6) * mm});
            skLineSegment(sketch, "E516", {"start": v(3.52, -7.6) * mm, "end": v(3.5, -7.66) * mm});
            skLineSegment(sketch, "E517", {"start": v(3.5, -7.66) * mm, "end": v(3.48, -7.72) * mm});
            skLineSegment(sketch, "E518", {"start": v(3.48, -7.72) * mm, "end": v(3.46, -7.78) * mm});
            skLineSegment(sketch, "E519", {"start": v(3.46, -7.78) * mm, "end": v(3.43, -7.83) * mm});
            skLineSegment(sketch, "E520", {"start": v(3.43, -7.83) * mm, "end": v(3.4, -7.87) * mm});
            skLineSegment(sketch, "E521", {"start": v(3.4, -7.87) * mm, "end": v(3.38, -7.92) * mm});
            skLineSegment(sketch, "E522", {"start": v(3.38, -7.92) * mm, "end": v(3.35, -7.95) * mm});
            skLineSegment(sketch, "E523", {"start": v(3.35, -7.95) * mm, "end": v(3.32, -7.99) * mm});
            skLineSegment(sketch, "E524", {"start": v(3.32, -7.99) * mm, "end": v(3.28, -8.02) * mm});
            skLineSegment(sketch, "E525", {"start": v(3.28, -8.02) * mm, "end": v(3.25, -8.05) * mm});
            skLineSegment(sketch, "E526", {"start": v(3.25, -8.05) * mm, "end": v(3.21, -8.07) * mm});
            skLineSegment(sketch, "E527", {"start": v(3.21, -8.07) * mm, "end": v(3.17, -8.09) * mm});
            skLineSegment(sketch, "E528", {"start": v(3.17, -8.09) * mm, "end": v(3.14, -8.1) * mm});
            skLineSegment(sketch, "E529", {"start": v(3.14, -8.1) * mm, "end": v(3.1, -8.12) * mm});
            skLineSegment(sketch, "E530", {"start": v(3.1, -8.12) * mm, "end": v(3.05, -8.13) * mm});
            skLineSegment(sketch, "E531", {"start": v(3.05, -8.13) * mm, "end": v(3.01, -8.14) * mm});
            skLineSegment(sketch, "E532", {"start": v(3.01, -8.14) * mm, "end": v(2.93, -8.14) * mm});
            skLineSegment(sketch, "E533", {"start": v(2.93, -8.14) * mm, "end": v(2.85, -8.14) * mm});
            skLineSegment(sketch, "E534", {"start": v(2.85, -8.14) * mm, "end": v(2.78, -8.12) * mm});
            skLineSegment(sketch, "E535", {"start": v(2.78, -8.12) * mm, "end": v(2.7, -8.1) * mm});
            skLineSegment(sketch, "E536", {"start": v(2.7, -8.1) * mm, "end": v(2.66, -8.08) * mm});
            skLineSegment(sketch, "E537", {"start": v(2.66, -8.08) * mm, "end": v(2.63, -8.06) * mm});
            skLineSegment(sketch, "E538", {"start": v(2.63, -8.06) * mm, "end": v(2.59, -8.04) * mm});
            skLineSegment(sketch, "E539", {"start": v(2.59, -8.04) * mm, "end": v(2.55, -8.02) * mm});
            skLineSegment(sketch, "E540", {"start": v(2.55, -8.02) * mm, "end": v(2.52, -7.99) * mm});
            skLineSegment(sketch, "E541", {"start": v(2.52, -7.99) * mm, "end": v(2.49, -7.95) * mm});
            skLineSegment(sketch, "E542", {"start": v(2.49, -7.95) * mm, "end": v(2.46, -7.91) * mm});
            skLineSegment(sketch, "E543", {"start": v(2.46, -7.91) * mm, "end": v(2.43, -7.87) * mm});
            skLineSegment(sketch, "E544", {"start": v(2.43, -7.87) * mm, "end": v(2.4, -7.83) * mm});
            skLineSegment(sketch, "E545", {"start": v(2.4, -7.83) * mm, "end": v(2.38, -7.77) * mm});
            skLineSegment(sketch, "E546", {"start": v(2.38, -7.77) * mm, "end": v(2.36, -7.72) * mm});
            skLineSegment(sketch, "E547", {"start": v(2.36, -7.72) * mm, "end": v(2.34, -7.66) * mm});
            skLineSegment(sketch, "E548", {"start": v(2.34, -7.66) * mm, "end": v(2.32, -7.59) * mm});
            skLineSegment(sketch, "E549", {"start": v(2.32, -7.59) * mm, "end": v(2.3, -7.52) * mm});
            skLineSegment(sketch, "E550", {"start": v(2.3, -7.52) * mm, "end": v(2.3, -7.44) * mm});
            skLineSegment(sketch, "E551", {"start": v(2.3, -7.44) * mm, "end": v(2.3, -7.36) * mm});
            skLineSegment(sketch, "E552", {"start": v(2.3, -7.36) * mm, "end": v(2.29, -7.2) * mm});
            skLineSegment(sketch, "E553", {"start": v(2.29, -7.2) * mm, "end": v(2.29, -4.58) * mm});
            skLineSegment(sketch, "E554", {"start": v(2.29, -4.58) * mm, "end": v(2.28, -4.56) * mm});
            skLineSegment(sketch, "E555", {"start": v(2.28, -4.56) * mm, "end": v(-1.57, -4.56) * mm});
            skLineSegment(sketch, "E556", {"start": v(-1.57, -4.56) * mm, "end": v(-1.6, -4.63) * mm});
            skLineSegment(sketch, "E557", {"start": v(-1.6, -4.63) * mm, "end": v(-1.58, -5.69) * mm});
            skLineSegment(sketch, "E558", {"start": v(-1.58, -5.69) * mm, "end": v(-1.56, -6.25) * mm});
            skLineSegment(sketch, "E559", {"start": v(-1.56, -6.25) * mm, "end": v(-1.54, -6.65) * mm});
            skLineSegment(sketch, "E560", {"start": v(-1.54, -6.65) * mm, "end": v(-1.5, -7.04) * mm});
            skLineSegment(sketch, "E561", {"start": v(-1.5, -7.04) * mm, "end": v(-1.48, -7.28) * mm});
            skLineSegment(sketch, "E562", {"start": v(-1.48, -7.28) * mm, "end": v(-1.44, -7.5) * mm});
            skLineSegment(sketch, "E563", {"start": v(-1.44, -7.5) * mm, "end": v(-1.4, -7.73) * mm});
            skLineSegment(sketch, "E564", {"start": v(-1.4, -7.73) * mm, "end": v(-1.36, -7.93) * mm});
            skLineSegment(sketch, "E565", {"start": v(-1.36, -7.93) * mm, "end": v(-1.27, -8.29) * mm});
            skLineSegment(sketch, "E566", {"start": v(-1.27, -8.29) * mm, "end": v(-1.16, -8.62) * mm});
            skLineSegment(sketch, "E567", {"start": v(-1.16, -8.62) * mm, "end": v(-1.05, -8.93) * mm});
            skLineSegment(sketch, "E568", {"start": v(-1.05, -8.93) * mm, "end": v(-0.93, -9.2) * mm});
            skLineSegment(sketch, "E569", {"start": v(-0.93, -9.2) * mm, "end": v(-0.8, -9.47) * mm});
            skLineSegment(sketch, "E570", {"start": v(-0.8, -9.47) * mm, "end": v(-0.66, -9.71) * mm});
            skLineSegment(sketch, "E571", {"start": v(-0.66, -9.71) * mm, "end": v(-0.5, -9.93) * mm});
            skLineSegment(sketch, "E572", {"start": v(-0.5, -9.93) * mm, "end": v(-0.35, -10.13) * mm});
            skLineSegment(sketch, "E573", {"start": v(-0.35, -10.13) * mm, "end": v(-0.18, -10.31) * mm});
            skLineSegment(sketch, "E574", {"start": v(-0.18, -10.31) * mm, "end": v(-0.01, -10.48) * mm});
            skLineSegment(sketch, "E575", {"start": v(-0.01, -10.48) * mm, "end": v(0.17, -10.63) * mm});
            skLineSegment(sketch, "E576", {"start": v(0.17, -10.63) * mm, "end": v(0.35, -10.76) * mm});
            skLineSegment(sketch, "E577", {"start": v(0.35, -10.76) * mm, "end": v(0.54, -10.87) * mm});
            skLineSegment(sketch, "E578", {"start": v(0.54, -10.87) * mm, "end": v(0.74, -10.97) * mm});
            skLineSegment(sketch, "E579", {"start": v(0.74, -10.97) * mm, "end": v(0.94, -11.06) * mm});
            skLineSegment(sketch, "E580", {"start": v(0.94, -11.06) * mm, "end": v(1.15, -11.13) * mm});
            skLineSegment(sketch, "E581", {"start": v(1.15, -11.13) * mm, "end": v(1.36, -11.2) * mm});
            skLineSegment(sketch, "E582", {"start": v(1.36, -11.2) * mm, "end": v(1.57, -11.25) * mm});
            skLineSegment(sketch, "E583", {"start": v(1.57, -11.25) * mm, "end": v(1.78, -11.29) * mm});
            skLineSegment(sketch, "E584", {"start": v(1.78, -11.29) * mm, "end": v(2, -11.32) * mm});
            skLineSegment(sketch, "E585", {"start": v(2, -11.32) * mm, "end": v(2.22, -11.34) * mm});
            skLineSegment(sketch, "E586", {"start": v(2.22, -11.34) * mm, "end": v(2.44, -11.35) * mm});
            skLineSegment(sketch, "E587", {"start": v(2.44, -11.35) * mm, "end": v(2.66, -11.36) * mm});
            skLineSegment(sketch, "E588", {"start": v(-10.1, -15.07) * mm, "end": v(-9.96, -15.06) * mm});
            skLineSegment(sketch, "E589", {"start": v(-9.96, -15.06) * mm, "end": v(-3.09, -15.06) * mm});
            skLineSegment(sketch, "E590", {"start": v(-3.09, -15.06) * mm, "end": v(-2.91, -15.05) * mm});
            skLineSegment(sketch, "E591", {"start": v(-2.91, -15.05) * mm, "end": v(-2.92, -2.66) * mm});
            skLineSegment(sketch, "E592", {"start": v(-2.92, -2.66) * mm, "end": v(-12.55, -3.56) * mm});
            skLineSegment(sketch, "E593", {"start": v(-12.55, -3.56) * mm, "end": v(-12.53, -3.6) * mm});
            skLineSegment(sketch, "E594", {"start": v(-12.53, -3.6) * mm, "end": v(-12.5, -3.64) * mm});
            skLineSegment(sketch, "E595", {"start": v(-12.5, -3.64) * mm, "end": v(-12.45, -3.69) * mm});
            skLineSegment(sketch, "E596", {"start": v(-12.45, -3.69) * mm, "end": v(-12.32, -3.79) * mm});
            skLineSegment(sketch, "E597", {"start": v(-12.32, -3.79) * mm, "end": v(-12.18, -3.9) * mm});
            skLineSegment(sketch, "E598", {"start": v(-12.18, -3.9) * mm, "end": v(-11.23, -4.54) * mm});
            skLineSegment(sketch, "E599", {"start": v(-11.23, -4.54) * mm, "end": v(-11.15, -4.6) * mm});
            skLineSegment(sketch, "E600", {"start": v(-11.15, -4.6) * mm, "end": v(-11.12, -4.63) * mm});
            skLineSegment(sketch, "E601", {"start": v(-11.12, -4.63) * mm, "end": v(-11.1, -4.64) * mm});
            skLineSegment(sketch, "E602", {"start": v(-11.1, -4.64) * mm, "end": v(-11.1, -4.66) * mm});
            skLineSegment(sketch, "E603", {"start": v(-11.1, -4.66) * mm, "end": v(-11.31, -4.67) * mm});
            skLineSegment(sketch, "E604", {"start": v(-11.31, -4.67) * mm, "end": v(-11.58, -4.7) * mm});
            skLineSegment(sketch, "E605", {"start": v(-11.58, -4.7) * mm, "end": v(-11.82, -4.77) * mm});
            skLineSegment(sketch, "E606", {"start": v(-11.82, -4.77) * mm, "end": v(-12.04, -4.86) * mm});
            skLineSegment(sketch, "E607", {"start": v(-12.04, -4.86) * mm, "end": v(-12.24, -4.98) * mm});
            skLineSegment(sketch, "E608", {"start": v(-12.24, -4.98) * mm, "end": v(-12.42, -5.11) * mm});
            skLineSegment(sketch, "E609", {"start": v(-12.42, -5.11) * mm, "end": v(-12.58, -5.26) * mm});
            skLineSegment(sketch, "E610", {"start": v(-12.58, -5.26) * mm, "end": v(-12.72, -5.43) * mm});
            skLineSegment(sketch, "E611", {"start": v(-12.72, -5.43) * mm, "end": v(-12.84, -5.6) * mm});
            skLineSegment(sketch, "E612", {"start": v(-12.84, -5.6) * mm, "end": v(-12.95, -5.8) * mm});
            skLineSegment(sketch, "E613", {"start": v(-12.95, -5.8) * mm, "end": v(-13.05, -6) * mm});
            skLineSegment(sketch, "E614", {"start": v(-13.05, -6) * mm, "end": v(-13.13, -6.19) * mm});
            skLineSegment(sketch, "E615", {"start": v(-13.13, -6.19) * mm, "end": v(-13.2, -6.39) * mm});
            skLineSegment(sketch, "E616", {"start": v(-13.2, -6.39) * mm, "end": v(-13.25, -6.58) * mm});
            skLineSegment(sketch, "E617", {"start": v(-13.25, -6.58) * mm, "end": v(-13.3, -6.78) * mm});
            skLineSegment(sketch, "E618", {"start": v(-13.3, -6.78) * mm, "end": v(-13.34, -6.96) * mm});
            skLineSegment(sketch, "E619", {"start": v(-13.34, -6.96) * mm, "end": v(-13.37, -7.14) * mm});
            skLineSegment(sketch, "E620", {"start": v(-13.37, -7.14) * mm, "end": v(-13.39, -7.3) * mm});
            skLineSegment(sketch, "E621", {"start": v(-13.39, -7.3) * mm, "end": v(-13.4, -7.45) * mm});
            skLineSegment(sketch, "E622", {"start": v(-13.4, -7.45) * mm, "end": v(-13.42, -7.69) * mm});
            skLineSegment(sketch, "E623", {"start": v(-13.42, -7.69) * mm, "end": v(-13.42, -7.8) * mm});
            skLineSegment(sketch, "E624", {"start": v(-13.42, -7.8) * mm, "end": v(-13.42, -10.7) * mm});
            skLineSegment(sketch, "E625", {"start": v(-13.42, -10.7) * mm, "end": v(-13.42, -11.23) * mm});
            skLineSegment(sketch, "E626", {"start": v(-13.42, -11.23) * mm, "end": v(-13.39, -11.73) * mm});
            skLineSegment(sketch, "E627", {"start": v(-13.39, -11.73) * mm, "end": v(-13.33, -12.18) * mm});
            skLineSegment(sketch, "E628", {"start": v(-13.33, -12.18) * mm, "end": v(-13.24, -12.59) * mm});
            skLineSegment(sketch, "E629", {"start": v(-13.24, -12.59) * mm, "end": v(-13.12, -12.95) * mm});
            skLineSegment(sketch, "E630", {"start": v(-13.12, -12.95) * mm, "end": v(-12.98, -13.28) * mm});
            skLineSegment(sketch, "E631", {"start": v(-12.98, -13.28) * mm, "end": v(-12.82, -13.58) * mm});
            skLineSegment(sketch, "E632", {"start": v(-12.82, -13.58) * mm, "end": v(-12.65, -13.83) * mm});
            skLineSegment(sketch, "E633", {"start": v(-12.65, -13.83) * mm, "end": v(-12.46, -14.06) * mm});
            skLineSegment(sketch, "E634", {"start": v(-12.46, -14.06) * mm, "end": v(-12.26, -14.26) * mm});
            skLineSegment(sketch, "E635", {"start": v(-12.26, -14.26) * mm, "end": v(-12.05, -14.43) * mm});
            skLineSegment(sketch, "E636", {"start": v(-12.05, -14.43) * mm, "end": v(-11.84, -14.57) * mm});
            skLineSegment(sketch, "E637", {"start": v(-11.84, -14.57) * mm, "end": v(-11.63, -14.7) * mm});
            skLineSegment(sketch, "E638", {"start": v(-11.63, -14.7) * mm, "end": v(-11.41, -14.8) * mm});
            skLineSegment(sketch, "E639", {"start": v(-11.41, -14.8) * mm, "end": v(-11.2, -14.88) * mm});
            skLineSegment(sketch, "E640", {"start": v(-11.2, -14.88) * mm, "end": v(-11, -14.94) * mm});
            skLineSegment(sketch, "E641", {"start": v(-11, -14.94) * mm, "end": v(-10.81, -14.99) * mm});
            skLineSegment(sketch, "E642", {"start": v(-10.81, -14.99) * mm, "end": v(-10.63, -15.02) * mm});
            skLineSegment(sketch, "E643", {"start": v(-10.63, -15.02) * mm, "end": v(-10.47, -15.04) * mm});
            skLineSegment(sketch, "E644", {"start": v(-10.47, -15.04) * mm, "end": v(-10.32, -15.06) * mm});
            skLineSegment(sketch, "E645", {"start": v(-10.32, -15.06) * mm, "end": v(-10.2, -15.06) * mm});
            skLineSegment(sketch, "E646", {"start": v(-10.2, -15.06) * mm, "end": v(-10.1, -15.07) * mm});
            skLineSegment(sketch, "E647", {"start": v(-7.4, -11.33) * mm, "end": v(-8.07, -11.33) * mm});
            skLineSegment(sketch, "E648", {"start": v(-8.07, -11.33) * mm, "end": v(-8.14, -11.32) * mm});
            skLineSegment(sketch, "E649", {"start": v(-8.14, -11.32) * mm, "end": v(-8.23, -11.3) * mm});
            skLineSegment(sketch, "E650", {"start": v(-8.23, -11.3) * mm, "end": v(-8.33, -11.27) * mm});
            skLineSegment(sketch, "E651", {"start": v(-8.33, -11.27) * mm, "end": v(-8.39, -11.25) * mm});
            skLineSegment(sketch, "E652", {"start": v(-8.39, -11.25) * mm, "end": v(-8.44, -11.22) * mm});
            skLineSegment(sketch, "E653", {"start": v(-8.44, -11.22) * mm, "end": v(-8.5, -11.18) * mm});
            skLineSegment(sketch, "E654", {"start": v(-8.5, -11.18) * mm, "end": v(-8.56, -11.14) * mm});
            skLineSegment(sketch, "E655", {"start": v(-8.56, -11.14) * mm, "end": v(-8.62, -11.1) * mm});
            skLineSegment(sketch, "E656", {"start": v(-8.62, -11.1) * mm, "end": v(-8.67, -11.05) * mm});
            skLineSegment(sketch, "E657", {"start": v(-8.67, -11.05) * mm, "end": v(-8.73, -10.99) * mm});
            skLineSegment(sketch, "E658", {"start": v(-8.73, -10.99) * mm, "end": v(-8.78, -10.92) * mm});
            skLineSegment(sketch, "E659", {"start": v(-8.78, -10.92) * mm, "end": v(-8.83, -10.84) * mm});
            skLineSegment(sketch, "E660", {"start": v(-8.83, -10.84) * mm, "end": v(-8.87, -10.76) * mm});
            skLineSegment(sketch, "E661", {"start": v(-8.87, -10.76) * mm, "end": v(-8.91, -10.67) * mm});
            skLineSegment(sketch, "E662", {"start": v(-8.91, -10.67) * mm, "end": v(-8.95, -10.57) * mm});
            skLineSegment(sketch, "E663", {"start": v(-8.95, -10.57) * mm, "end": v(-8.98, -10.46) * mm});
            skLineSegment(sketch, "E664", {"start": v(-8.98, -10.46) * mm, "end": v(-9, -10.34) * mm});
            skLineSegment(sketch, "E665", {"start": v(-9, -10.34) * mm, "end": v(-9.02, -10.2) * mm});
            skLineSegment(sketch, "E666", {"start": v(-9.02, -10.2) * mm, "end": v(-9.03, -10.06) * mm});
            skLineSegment(sketch, "E667", {"start": v(-9.03, -10.06) * mm, "end": v(-9.03, -7.5) * mm});
            skLineSegment(sketch, "E668", {"start": v(-9.03, -7.5) * mm, "end": v(-9, -7.22) * mm});
            skLineSegment(sketch, "E669", {"start": v(-9, -7.22) * mm, "end": v(-8.99, -7.07) * mm});
            skLineSegment(sketch, "E670", {"start": v(-8.99, -7.07) * mm, "end": v(-8.95, -6.9) * mm});
            skLineSegment(sketch, "E671", {"start": v(-8.95, -6.9) * mm, "end": v(-8.93, -6.8) * mm});
            skLineSegment(sketch, "E672", {"start": v(-8.93, -6.8) * mm, "end": v(-8.9, -6.72) * mm});
            skLineSegment(sketch, "E673", {"start": v(-8.9, -6.72) * mm, "end": v(-8.88, -6.63) * mm});
            skLineSegment(sketch, "E674", {"start": v(-8.88, -6.63) * mm, "end": v(-8.84, -6.54) * mm});
            skLineSegment(sketch, "E675", {"start": v(-8.84, -6.54) * mm, "end": v(-8.8, -6.45) * mm});
            skLineSegment(sketch, "E676", {"start": v(-8.8, -6.45) * mm, "end": v(-8.76, -6.37) * mm});
            skLineSegment(sketch, "E677", {"start": v(-8.76, -6.37) * mm, "end": v(-8.7, -6.3) * mm});
            skLineSegment(sketch, "E678", {"start": v(-8.7, -6.3) * mm, "end": v(-8.65, -6.22) * mm});
            skLineSegment(sketch, "E679", {"start": v(-8.65, -6.22) * mm, "end": v(-8.58, -6.15) * mm});
            skLineSegment(sketch, "E680", {"start": v(-8.58, -6.15) * mm, "end": v(-8.51, -6.1) * mm});
            skLineSegment(sketch, "E681", {"start": v(-8.51, -6.1) * mm, "end": v(-8.43, -6.05) * mm});
            skLineSegment(sketch, "E682", {"start": v(-8.43, -6.05) * mm, "end": v(-8.34, -6) * mm});
            skLineSegment(sketch, "E683", {"start": v(-8.34, -6) * mm, "end": v(-8.25, -5.97) * mm});
            skLineSegment(sketch, "E684", {"start": v(-8.25, -5.97) * mm, "end": v(-8.15, -5.96) * mm});
            skLineSegment(sketch, "E685", {"start": v(-8.15, -5.96) * mm, "end": v(-8.03, -5.95) * mm});
            skLineSegment(sketch, "E686", {"start": v(-8.03, -5.95) * mm, "end": v(-7.4, -5.95) * mm});
            skLineSegment(sketch, "E687", {"start": v(-7.4, -5.95) * mm, "end": v(-7.4, -11.33) * mm});
            skLineSegment(sketch, "E688", {"start": v(-16.9, -11) * mm, "end": v(-16.17, -3.8) * mm});
            skLineSegment(sketch, "E689", {"start": v(-16.17, -3.8) * mm, "end": v(-19.57, -3.88) * mm});
            skLineSegment(sketch, "E690", {"start": v(-19.57, -3.88) * mm, "end": v(-19.58, -3.98) * mm});
            skLineSegment(sketch, "E691", {"start": v(-19.58, -3.98) * mm, "end": v(-19.77, -7.67) * mm});
            skLineSegment(sketch, "E692", {"start": v(-19.77, -7.67) * mm, "end": v(-19.9, -6.1) * mm});
            skLineSegment(sketch, "E693", {"start": v(-19.9, -6.1) * mm, "end": v(-20.04, -4.03) * mm});
            skLineSegment(sketch, "E694", {"start": v(-20.04, -4.03) * mm, "end": v(-20.07, -3.9) * mm});
            skLineSegment(sketch, "E695", {"start": v(-20.07, -3.9) * mm, "end": v(-20.35, -3.9) * mm});
            skLineSegment(sketch, "E696", {"start": v(-20.35, -3.9) * mm, "end": v(-23.3, -3.8) * mm});
            skLineSegment(sketch, "E697", {"start": v(-23.3, -3.8) * mm, "end": v(-23.3, -3.85) * mm});
            skLineSegment(sketch, "E698", {"start": v(-23.3, -3.85) * mm, "end": v(-22.27, -10.87) * mm});
            skLineSegment(sketch, "E699", {"start": v(-22.27, -10.87) * mm, "end": v(-22.23, -11) * mm});
            skLineSegment(sketch, "E700", {"start": v(-22.23, -11) * mm, "end": v(-17.04, -11) * mm});
            skLineSegment(sketch, "E701", {"start": v(-17.04, -11) * mm, "end": v(-16.9, -11) * mm});
            skSolve(sketch);
        }
        {
            var Q0;
            Q0=qSketchRegion(id+"F4",true);
            extrude(context, id + "F5", {"entities" : qUnion([Q0]), "operationType" : NewBodyOperationType.REMOVE, "oppositeDirection" : true, "depth" : 1 * mm});
        }
        {
            var Q0;
            Q0=makeQuery(id+"F1.opExtrude","CAP_FACE",FACE,{"disambiguationData":[OSD([sQuery(id+"F0.wireOp",EDGE,"E1.filletArc"),sQuery(id+"F0.wireOp",EDGE,"E2.filletArc"),sQuery(id+"F0.wireOp",EDGE,"E3.filletArc"),sQuery(id+"F0.wireOp",EDGE,"E4.filletArc"),sQuery(id+"F0.wireOp",EDGE,"E0.bottom"),sQuery(id+"F0.wireOp",EDGE,"E0.top"),sQuery(id+"F0.wireOp",EDGE,"E0.left"),sQuery(id+"F0.wireOp",EDGE,"E0.right")])],"isStart":true});
            var sketch = newSketch(context, id + "F6", { "sketchPlane" : qUnion([Q0])});
            skLineSegment(sketch, "E702.bottom", {"start": v(-48.27, 25.16) * mm, "end": v(-45.1, 25.16) * mm});
            skLineSegment(sketch, "E702.top", {"start": v(-48.27, -28.82) * mm, "end": v(-45.1, -28.82) * mm});
            skLineSegment(sketch, "E702.left", {"start": v(-48.27, 25.16) * mm, "end": v(-48.27, -25.64) * mm});
            skLineSegment(sketch, "E702.right", {"start": v(-45.1, 25.16) * mm, "end": v(-45.1, -28.82) * mm});
            skLineSegment(sketch, "E703.bottom", {"start": v(-48.27, -28.82) * mm, "end": v(46.98, -28.82) * mm});
            skLineSegment(sketch, "E703.top", {"start": v(-48.27, -25.64) * mm, "end": v(46.98, -25.64) * mm});
            skLineSegment(sketch, "E703.left", {"start": v(-48.27, -28.82) * mm, "end": v(-48.27, -25.64) * mm});
            skLineSegment(sketch, "E703.right", {"start": v(46.98, -28.82) * mm, "end": v(46.98, -25.64) * mm});
            skLineSegment(sketch, "E704.bottom", {"start": v(46.98, 25.16) * mm, "end": v(43.8, 25.16) * mm});
            skLineSegment(sketch, "E704.top", {"start": v(46.98, -28.82) * mm, "end": v(43.8, -28.82) * mm});
            skLineSegment(sketch, "E704.left", {"start": v(46.98, 25.16) * mm, "end": v(46.98, -28.82) * mm});
            skLineSegment(sketch, "E704.right", {"start": v(43.8, 25.16) * mm, "end": v(43.8, -28.82) * mm});
            skSolve(sketch);
        }
        {
            var Q0;
            {var subQ5=sQuery(id+"F6.wireOp",EDGE,"E702.bottom");Q0=makeQuery(id+"F6.imprint","IMPRINT",FACE,{"disambiguationData":[TD([[makeQuery(id+"F6.imprint","IMPRINT",EDGE,{"derivedFrom":subQ5}),-1.0]])]});}
            var Q1;
            {var subQ0=sQuery(id+"F0.wireOp",EDGE,"E3.filletArc");var subQ1=makeQuery(id+"F2.opFillet","BLEND_EDGE",EDGE,{"blendedFrom":[makeQuery(id+"F1.opExtrude","CAP_EDGE",EDGE,{"disambiguationData":[OSD([subQ0])],"isStart":false}),makeQuery(id+"F1.opExtrude","CAP_FACE",FACE,{"disambiguationData":[OSD([sQuery(id+"F0.wireOp",EDGE,"E1.filletArc"),sQuery(id+"F0.wireOp",EDGE,"E2.filletArc"),subQ0,sQuery(id+"F0.wireOp",EDGE,"E4.filletArc"),sQuery(id+"F0.wireOp",EDGE,"E0.bottom"),sQuery(id+"F0.wireOp",EDGE,"E0.top"),sQuery(id+"F0.wireOp",EDGE,"E0.left"),sQuery(id+"F0.wireOp",EDGE,"E0.right")])],"isStart":true})],"blendedInto":[makeQuery(id+"F1.opExtrude","CAP_FACE",FACE,{"disambiguationData":[OSD([sQuery(id+"F0.wireOp",EDGE,"E1.filletArc"),sQuery(id+"F0.wireOp",EDGE,"E2.filletArc"),subQ0,sQuery(id+"F0.wireOp",EDGE,"E4.filletArc"),sQuery(id+"F0.wireOp",EDGE,"E0.bottom"),sQuery(id+"F0.wireOp",EDGE,"E0.top"),sQuery(id+"F0.wireOp",EDGE,"E0.left"),sQuery(id+"F0.wireOp",EDGE,"E0.right")])],"isStart":true})]});Q1=makeQuery(id+"F6.imprint","IMPRINT",FACE,{"disambiguationData":[TD([[makeQuery(id+"F6.imprint","IMPRINT",EDGE,{"derivedFrom":subQ1}),-1.0]])]});}
            var Q2;
            {var subQ1=sQuery(id+"F6.wireOp",EDGE,"E703.top");var subQ8=sQuery(id+"F6.wireOp",EDGE,"E702.right");var subQ9=makeQuery(id+"F6.imprint","INTERSECT",VERTEX,{"derivedFrom":[subQ8,subQ1]});Q2=makeQuery(id+"F6.imprint","IMPRINT",FACE,{"disambiguationData":[TD([[makeQuery(id+"F6.imprint","IMPRINT",EDGE,{"disambiguationData":[TD([[subQ9,-1.0]])],"derivedFrom":subQ1}),-1.0]])]});}
            var Q3;
            {var subQ0=sQuery(id+"F0.wireOp",EDGE,"E4.filletArc");var subQ1=makeQuery(id+"F2.opFillet","BLEND_EDGE",EDGE,{"blendedFrom":[makeQuery(id+"F1.opExtrude","CAP_EDGE",EDGE,{"disambiguationData":[OSD([subQ0])],"isStart":false}),makeQuery(id+"F1.opExtrude","CAP_FACE",FACE,{"disambiguationData":[OSD([sQuery(id+"F0.wireOp",EDGE,"E1.filletArc"),sQuery(id+"F0.wireOp",EDGE,"E2.filletArc"),sQuery(id+"F0.wireOp",EDGE,"E3.filletArc"),subQ0,sQuery(id+"F0.wireOp",EDGE,"E0.bottom"),sQuery(id+"F0.wireOp",EDGE,"E0.top"),sQuery(id+"F0.wireOp",EDGE,"E0.left"),sQuery(id+"F0.wireOp",EDGE,"E0.right")])],"isStart":true})],"blendedInto":[makeQuery(id+"F1.opExtrude","CAP_FACE",FACE,{"disambiguationData":[OSD([sQuery(id+"F0.wireOp",EDGE,"E1.filletArc"),sQuery(id+"F0.wireOp",EDGE,"E2.filletArc"),sQuery(id+"F0.wireOp",EDGE,"E3.filletArc"),subQ0,sQuery(id+"F0.wireOp",EDGE,"E0.bottom"),sQuery(id+"F0.wireOp",EDGE,"E0.top"),sQuery(id+"F0.wireOp",EDGE,"E0.left"),sQuery(id+"F0.wireOp",EDGE,"E0.right")])],"isStart":true})]});Q3=makeQuery(id+"F6.imprint","IMPRINT",FACE,{"disambiguationData":[TD([[makeQuery(id+"F6.imprint","IMPRINT",EDGE,{"derivedFrom":subQ1}),-1.0]])]});}
            var Q4;
            {var subQ3=sQuery(id+"F6.wireOp",EDGE,"E704.bottom");Q4=makeQuery(id+"F6.imprint","IMPRINT",FACE,{"disambiguationData":[TD([[makeQuery(id+"F6.imprint","IMPRINT",EDGE,{"derivedFrom":subQ3}),1.0]])]});}
            extrude(context, id + "F7", {"entities" : qUnion([Q0, Q1, Q2, Q3, Q4]), "depth" : 3.17 * mm});
        }
        {
            var Q0;
            Q0=makeQuery(id+"F7.opExtrude","CAP_FACE",FACE,{"disambiguationData":[OSD([sQuery(id+"F0.wireOp",EDGE,"E1.filletArc"),sQuery(id+"F0.wireOp",EDGE,"E2.filletArc"),sQuery(id+"F0.wireOp",EDGE,"E3.filletArc"),sQuery(id+"F0.wireOp",EDGE,"E4.filletArc"),sQuery(id+"F0.wireOp",EDGE,"E0.bottom"),sQuery(id+"F0.wireOp",EDGE,"E0.top"),sQuery(id+"F0.wireOp",EDGE,"E0.left"),sQuery(id+"F0.wireOp",EDGE,"E0.right"),sQuery(id+"F6.wireOp",EDGE,"E702.bottom"),sQuery(id+"F6.wireOp",EDGE,"E702.left"),sQuery(id+"F6.wireOp",EDGE,"E702.right"),sQuery(id+"F6.wireOp",EDGE,"E703.bottom"),sQuery(id+"F6.wireOp",EDGE,"E703.top"),sQuery(id+"F6.wireOp",EDGE,"E704.bottom"),sQuery(id+"F6.wireOp",EDGE,"E704.left"),sQuery(id+"F6.wireOp",EDGE,"E704.right")])],"isStart":false});
            var sketch = newSketch(context, id + "F8", { "sketchPlane" : qUnion([Q0])});
            skLineSegment(sketch, "E705.bottom", {"start": v(-48.27, 25.16) * mm, "end": v(46.98, 25.16) * mm});
            skLineSegment(sketch, "E705.top", {"start": v(-48.27, -28.82) * mm, "end": v(46.98, -28.82) * mm});
            skLineSegment(sketch, "E705.left", {"start": v(-48.27, 25.16) * mm, "end": v(-48.27, -28.82) * mm});
            skLineSegment(sketch, "E705.right", {"start": v(46.98, 25.16) * mm, "end": v(46.98, -28.82) * mm});
            skSolve(sketch);
        }
        {
            var Q0;
            {var subQ12=makeQuery(id+"F7.opExtrude","CAP_EDGE",EDGE,{"disambiguationData":[OSD([sQuery(id+"F6.wireOp",EDGE,"E702.right")])],"isStart":false});Q0=makeQuery(id+"F8.imprint","IMPRINT",FACE,{"disambiguationData":[TD([[makeQuery(id+"F8.imprint","IMPRINT",EDGE,{"derivedFrom":subQ12}),-1.0]])]});}
            var Q1;
            {var subQ1=makeQuery(id+"F7.opExtrude","CAP_EDGE",EDGE,{"disambiguationData":[OSD([sQuery(id+"F6.wireOp",EDGE,"E702.right")])],"isStart":false});Q1=makeQuery(id+"F8.imprint","IMPRINT",FACE,{"disambiguationData":[TD([[makeQuery(id+"F8.imprint","IMPRINT",EDGE,{"derivedFrom":subQ1}),1.0]])]});}
            extrude(context, id + "F9", {"entities" : qUnion([Q0, Q1]), "operationType" : NewBodyOperationType.ADD, "depth" : 2 * mm});
        }
        {
            var Q0;
            Q0=qCreatedBy(makeId("Top.planeOp"),FACE);
            cPlane(context, id + "F10", {"entities" : qUnion([Q0]), "cplaneType" : CPlaneType.OFFSET, "offset" : 2 * mm, "oppositeDirection" : true, "width" : 152.4 * mm, "height" : 152.4 * mm});
        }
        {
            var Q0;
            Q0=qCreatedBy(id+"F10.planeOp",FACE);
            var sketch = newSketch(context, id + "F11", { "sketchPlane" : qUnion([Q0])});
            skArc(sketch, "E706", {"start": v(65.1, -7.37) * mm, "mid": v(71.11, 0) * mm, "end": v(65.1, 7.37) * mm});
            skLineSegment(sketch, "E707", {"start": v(65.1, -7.37) * mm, "end": v(46.33, -25.13) * mm});
            skLineSegment(sketch, "E708", {"start": v(46.33, -25.13) * mm, "end": v(46.33, 25.84) * mm});
            skLineSegment(sketch, "E709", {"start": v(46.33, 25.84) * mm, "end": v(65.1, 7.37) * mm});
            skCircle(sketch, "E710", {"center": v(63.58, 0) * mm, "radius": 3.97 * mm});
            skLineSegment(sketch, "E711.bottom", {"start": v(39.4, 27.12) * mm, "end": v(46.94, 27.12) * mm});
            skLineSegment(sketch, "E711.top", {"start": v(39.4, -26.69) * mm, "end": v(46.94, -26.69) * mm});
            skLineSegment(sketch, "E711.left", {"start": v(39.4, 27.12) * mm, "end": v(39.4, -26.69) * mm});
            skLineSegment(sketch, "E711.right", {"start": v(46.94, 27.12) * mm, "end": v(46.94, -26.69) * mm});
            skSolve(sketch);
        }
        {
            var Q0;
            {var subQ5=sQuery(id+"F11.wireOp",EDGE,"E706");Q0=makeQuery(id+"F11.imprint","IMPRINT",FACE,{"disambiguationData":[TD([[makeQuery(id+"F11.imprint","IMPRINT",EDGE,{"derivedFrom":subQ5}),1.0]])]});}
            var Q1;
            Q1=makeQuery(id+"F9.opExtrude","CAP_FACE",FACE,{"disambiguationData":[OSD([sQuery(id+"F0.wireOp",EDGE,"E1.filletArc"),sQuery(id+"F0.wireOp",EDGE,"E2.filletArc"),sQuery(id+"F0.wireOp",EDGE,"E3.filletArc"),sQuery(id+"F0.wireOp",EDGE,"E4.filletArc"),sQuery(id+"F0.wireOp",EDGE,"E0.bottom"),sQuery(id+"F0.wireOp",EDGE,"E0.top"),sQuery(id+"F0.wireOp",EDGE,"E0.left"),sQuery(id+"F0.wireOp",EDGE,"E0.right"),sQuery(id+"F8.wireOp",EDGE,"E705.bottom"),sQuery(id+"F8.wireOp",EDGE,"E705.top"),sQuery(id+"F8.wireOp",EDGE,"E705.left"),sQuery(id+"F8.wireOp",EDGE,"E705.right")])],"isStart":false});
            extrude(context, id + "F12", {"entities" : qUnion([Q0]), "operationType" : NewBodyOperationType.ADD, "endBound" : BoundingType.UP_TO_SURFACE, "oppositeDirection" : true, "endBoundEntityFace" : qUnion([Q1]), "depth" : 4 * mm});
        }
        {
            var Q0;
            Q0=makeQuery(id+"F12.opExtrude","CAP_EDGE",EDGE,{"disambiguationData":[OSD([sQuery(id+"F11.wireOp",EDGE,"E707")])],"isStart":false});
            var Q1;
            Q1=makeQuery(id+"F12.opExtrude","CAP_EDGE",EDGE,{"disambiguationData":[OSD([sQuery(id+"F11.wireOp",EDGE,"E709")])],"isStart":false});
            fillet(context, id + "F13", {"entities" : qUnion([Q0, Q1]), "radius" : 1 * mm, "tangentPropagation" : true, "allowEdgeOverflow" : false});
        }
        {
            var Q0;
            Q0=makeQuery(id+"F12.opExtrude","CAP_EDGE",EDGE,{"disambiguationData":[OSD([sQuery(id+"F11.wireOp",EDGE,"E706")])],"isStart":false});
            fillet(context, id + "F14", {"entities" : qUnion([Q0]), "radius" : 1 * mm, "tangentPropagation" : true, "allowEdgeOverflow" : false});
        }
        {
            var Q0;
            Q0=makeQuery(id+"F12.opExtrude","CAP_EDGE",EDGE,{"disambiguationData":[OSD([sQuery(id+"F11.wireOp",EDGE,"E710")])],"isStart":false});
            fillet(context, id + "F15", {"entities" : qUnion([Q0]), "radius" : 2 * mm, "tangentPropagation" : true, "allowEdgeOverflow" : false});
        }
        {
            var Q0;
            Q0=makeQuery(id+"F9.opExtrude","CAP_FACE",FACE,{"disambiguationData":[OSD([sQuery(id+"F0.wireOp",EDGE,"E1.filletArc"),sQuery(id+"F0.wireOp",EDGE,"E2.filletArc"),sQuery(id+"F0.wireOp",EDGE,"E3.filletArc"),sQuery(id+"F0.wireOp",EDGE,"E4.filletArc"),sQuery(id+"F0.wireOp",EDGE,"E0.bottom"),sQuery(id+"F0.wireOp",EDGE,"E0.top"),sQuery(id+"F0.wireOp",EDGE,"E0.left"),sQuery(id+"F0.wireOp",EDGE,"E0.right"),sQuery(id+"F8.wireOp",EDGE,"E705.bottom"),sQuery(id+"F8.wireOp",EDGE,"E705.top"),sQuery(id+"F8.wireOp",EDGE,"E705.left"),sQuery(id+"F8.wireOp",EDGE,"E705.right")])],"isStart":false});
            fillet(context, id + "F16", {"entities" : qUnion([Q0]), "radius" : 1 * mm, "tangentPropagation" : true, "allowEdgeOverflow" : false});
        }
        {
            var Q0;
            Q0=makeQuery(id+"F9.opExtrude","CAP_FACE",FACE,{"disambiguationData":[OSD([sQuery(id+"F0.wireOp",EDGE,"E1.filletArc"),sQuery(id+"F0.wireOp",EDGE,"E2.filletArc"),sQuery(id+"F0.wireOp",EDGE,"E3.filletArc"),sQuery(id+"F0.wireOp",EDGE,"E4.filletArc"),sQuery(id+"F0.wireOp",EDGE,"E0.bottom"),sQuery(id+"F0.wireOp",EDGE,"E0.top"),sQuery(id+"F0.wireOp",EDGE,"E0.left"),sQuery(id+"F0.wireOp",EDGE,"E0.right"),sQuery(id+"F8.wireOp",EDGE,"E705.bottom"),sQuery(id+"F8.wireOp",EDGE,"E705.top"),sQuery(id+"F8.wireOp",EDGE,"E705.left"),sQuery(id+"F8.wireOp",EDGE,"E705.right")])],"isStart":false});
            var sketch = newSketch(context, id + "F17", { "sketchPlane" : qUnion([Q0])});
            skLineSegment(sketch, "E712.bottom", {"start": v(-42.13, 20.77) * mm, "end": v(40.27, 20.77) * mm});
            skLineSegment(sketch, "E712.top", {"start": v(-42.13, -24.27) * mm, "end": v(40.27, -24.27) * mm});
            skLineSegment(sketch, "E712.left", {"start": v(-42.13, 20.77) * mm, "end": v(-42.13, -24.27) * mm});
            skLineSegment(sketch, "E712.right", {"start": v(40.27, 20.77) * mm, "end": v(40.27, -24.27) * mm});
            skSolve(sketch);
        }
        {
            var Q0;
            Q0=makeQuery(id+"F17.imprint","IMPRINT",FACE,{"disambiguationData":[TD([[makeQuery(id+"F17.imprint","IMPRINT",EDGE,{"derivedFrom":sQuery(id+"F17.wireOp",EDGE,"E712.bottom")}),-1.0]])]});
            extrude(context, id + "F18", {"entities" : qUnion([Q0]), "operationType" : NewBodyOperationType.REMOVE, "oppositeDirection" : true, "depth" : 25.4 * mm});
        }
    });
